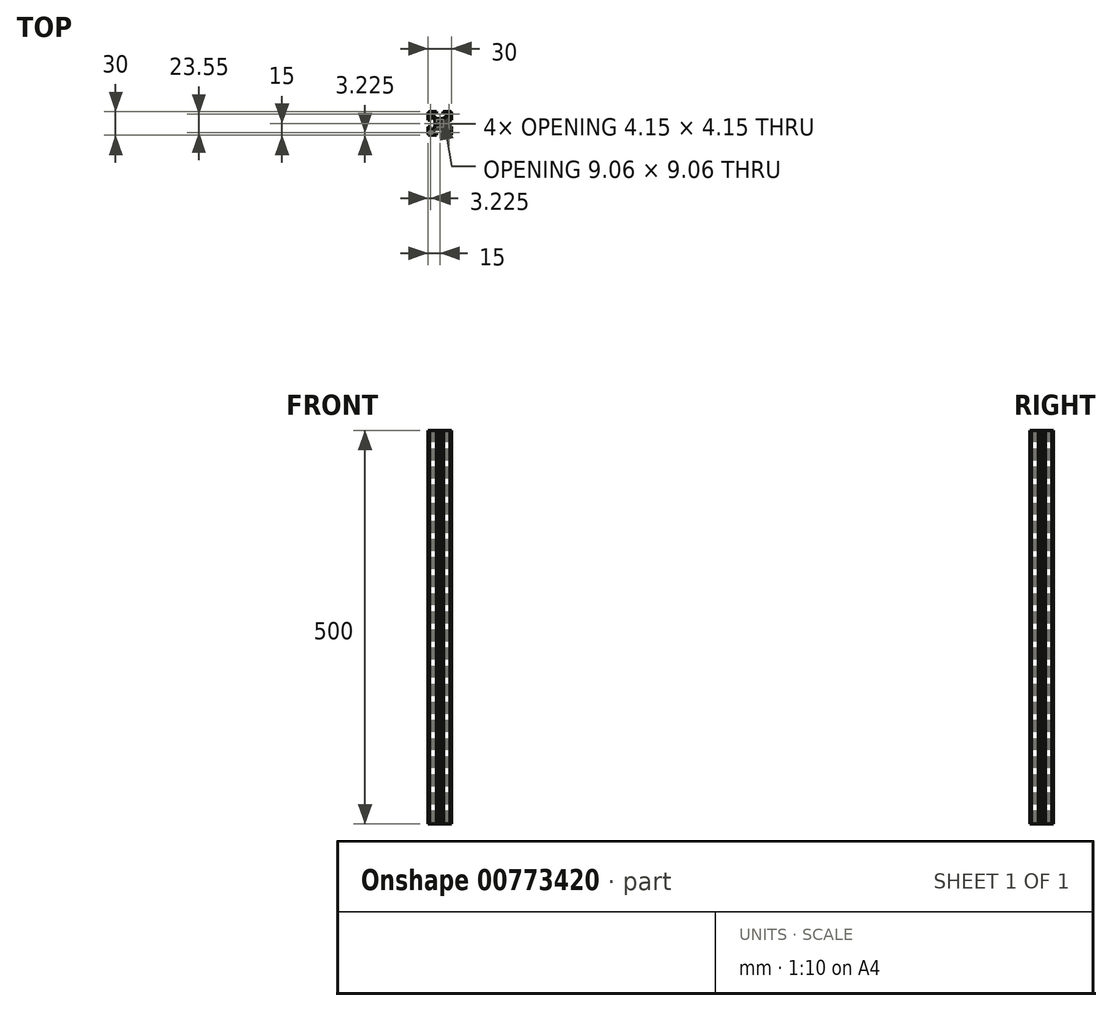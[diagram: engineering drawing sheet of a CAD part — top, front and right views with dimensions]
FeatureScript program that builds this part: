
annotation { "Feature Type Name" : "Feature", "Feature Type Description" : "" }
export const myFeature = defineFeature(function(context is Context, id is Id, definition is map)
    precondition{}
    {
        {
            var Q0;
            Q0=qCreatedBy(makeId("Top.planeOp"),FACE);
            var sketch = newSketch(context, id + "F0", { "sketchPlane" : qUnion([Q0])});
            skLineSegment(sketch, "E0", {"start": v(12.8, -8.25) * mm, "end": v(12.8, -4) * mm});
            skLineSegment(sketch, "E1", {"start": v(-12.8, 4) * mm, "end": v(-12.8, 8.25) * mm});
            skLineSegment(sketch, "E2", {"start": v(-13.85, -12.9) * mm, "end": v(-13.85, -12.85) * mm});
            skLineSegment(sketch, "E3", {"start": v(9.7, -12.9) * mm, "end": v(9.7, -12.85) * mm});
            skLineSegment(sketch, "E4", {"start": v(-9.7, -10.7) * mm, "end": v(-9.7, -10.66) * mm});
            skLineSegment(sketch, "E5", {"start": v(13.85, -10.7) * mm, "end": v(13.85, -10.66) * mm});
            skLineSegment(sketch, "E6", {"start": v(9.7, 10.66) * mm, "end": v(9.7, 10.7) * mm});
            skLineSegment(sketch, "E7", {"start": v(-13.85, 10.66) * mm, "end": v(-13.85, 10.7) * mm});
            skLineSegment(sketch, "E8", {"start": v(13.85, 12.85) * mm, "end": v(13.85, 12.9) * mm});
            skLineSegment(sketch, "E9", {"start": v(-9.7, 12.85) * mm, "end": v(-9.7, 12.9) * mm});
            skLineSegment(sketch, "E10", {"start": v(-15, -13.09) * mm, "end": v(-15, -13) * mm});
            skLineSegment(sketch, "E11", {"start": v(15, 13) * mm, "end": v(15, 13.09) * mm});
            skLineSegment(sketch, "E12", {"start": v(-3.64, -0.26) * mm, "end": v(-3.65, -0.09) * mm});
            skLineSegment(sketch, "E13", {"start": v(3.65, 0.09) * mm, "end": v(3.64, 0.26) * mm});
            skLineSegment(sketch, "E14", {"start": v(9.7, -12.94) * mm, "end": v(9.7, -12.9) * mm});
            skLineSegment(sketch, "E15", {"start": v(-9.7, -10.66) * mm, "end": v(-9.7, -10.61) * mm});
            skLineSegment(sketch, "E16", {"start": v(9.7, 10.61) * mm, "end": v(9.7, 10.66) * mm});
            skLineSegment(sketch, "E17", {"start": v(-9.7, 12.9) * mm, "end": v(-9.7, 12.94) * mm});
            skLineSegment(sketch, "E18", {"start": v(-15, -13.18) * mm, "end": v(-15, -13.09) * mm});
            skLineSegment(sketch, "E19", {"start": v(15, 13.09) * mm, "end": v(15, 13.18) * mm});
            skLineSegment(sketch, "E20", {"start": v(-13.85, -12.94) * mm, "end": v(-13.85, -12.9) * mm});
            skLineSegment(sketch, "E21", {"start": v(13.85, -10.66) * mm, "end": v(13.85, -10.61) * mm});
            skLineSegment(sketch, "E22", {"start": v(-13.85, 10.61) * mm, "end": v(-13.85, 10.66) * mm});
            skLineSegment(sketch, "E23", {"start": v(13.85, 12.9) * mm, "end": v(13.85, 12.94) * mm});
            skLineSegment(sketch, "E24", {"start": v(-3.62, -0.44) * mm, "end": v(-3.64, -0.26) * mm});
            skLineSegment(sketch, "E25", {"start": v(3.64, 0.26) * mm, "end": v(3.62, 0.44) * mm});
            skLineSegment(sketch, "E26", {"start": v(13.85, -10.61) * mm, "end": v(13.84, -10.57) * mm});
            skLineSegment(sketch, "E27", {"start": v(-13.84, 10.57) * mm, "end": v(-13.85, 10.61) * mm});
            skLineSegment(sketch, "E28", {"start": v(-13.84, -12.98) * mm, "end": v(-13.85, -12.94) * mm});
            skLineSegment(sketch, "E29", {"start": v(13.85, 12.94) * mm, "end": v(13.84, 12.98) * mm});
            skLineSegment(sketch, "E30", {"start": v(-14.98, -13.27) * mm, "end": v(-15, -13.18) * mm});
            skLineSegment(sketch, "E31", {"start": v(15, 13.18) * mm, "end": v(14.98, 13.27) * mm});
            skLineSegment(sketch, "E32", {"start": v(-9.7, -10.61) * mm, "end": v(-9.7, -10.57) * mm});
            skLineSegment(sketch, "E33", {"start": v(9.7, 10.57) * mm, "end": v(9.7, 10.61) * mm});
            skLineSegment(sketch, "E34", {"start": v(9.7, -12.98) * mm, "end": v(9.7, -12.94) * mm});
            skLineSegment(sketch, "E35", {"start": v(-9.7, 12.94) * mm, "end": v(-9.7, 12.98) * mm});
            skLineSegment(sketch, "E36", {"start": v(-3.6, -0.61) * mm, "end": v(-3.62, -0.44) * mm});
            skLineSegment(sketch, "E37", {"start": v(3.62, 0.44) * mm, "end": v(3.6, 0.61) * mm});
            skLineSegment(sketch, "E38", {"start": v(-13.83, -13.03) * mm, "end": v(-13.84, -12.98) * mm});
            skLineSegment(sketch, "E39", {"start": v(9.72, -13.03) * mm, "end": v(9.7, -12.98) * mm});
            skLineSegment(sketch, "E40", {"start": v(13.84, 12.98) * mm, "end": v(13.83, 13.03) * mm});
            skLineSegment(sketch, "E41", {"start": v(-9.7, 12.98) * mm, "end": v(-9.72, 13.03) * mm});
            skLineSegment(sketch, "E42", {"start": v(-14.97, -13.36) * mm, "end": v(-14.98, -13.27) * mm});
            skLineSegment(sketch, "E43", {"start": v(14.98, 13.27) * mm, "end": v(14.97, 13.36) * mm});
            skLineSegment(sketch, "E44", {"start": v(-9.7, -10.57) * mm, "end": v(-9.72, -10.52) * mm});
            skLineSegment(sketch, "E45", {"start": v(13.84, -10.57) * mm, "end": v(13.83, -10.52) * mm});
            skLineSegment(sketch, "E46", {"start": v(9.72, 10.52) * mm, "end": v(9.7, 10.57) * mm});
            skLineSegment(sketch, "E47", {"start": v(-13.83, 10.52) * mm, "end": v(-13.84, 10.57) * mm});
            skLineSegment(sketch, "E48", {"start": v(-3.56, -0.79) * mm, "end": v(-3.6, -0.61) * mm});
            skLineSegment(sketch, "E49", {"start": v(3.6, 0.61) * mm, "end": v(3.56, 0.79) * mm});
            skLineSegment(sketch, "E50", {"start": v(-14.95, -13.45) * mm, "end": v(-14.97, -13.36) * mm});
            skLineSegment(sketch, "E51", {"start": v(14.97, 13.36) * mm, "end": v(14.95, 13.45) * mm});
            skLineSegment(sketch, "E52", {"start": v(-13.82, -13.07) * mm, "end": v(-13.83, -13.03) * mm});
            skLineSegment(sketch, "E53", {"start": v(9.73, -13.07) * mm, "end": v(9.72, -13.03) * mm});
            skLineSegment(sketch, "E54", {"start": v(-9.72, -10.52) * mm, "end": v(-9.73, -10.48) * mm});
            skLineSegment(sketch, "E55", {"start": v(13.83, -10.52) * mm, "end": v(13.82, -10.48) * mm});
            skLineSegment(sketch, "E56", {"start": v(9.73, 10.48) * mm, "end": v(9.72, 10.52) * mm});
            skLineSegment(sketch, "E57", {"start": v(-13.82, 10.48) * mm, "end": v(-13.83, 10.52) * mm});
            skLineSegment(sketch, "E58", {"start": v(13.83, 13.03) * mm, "end": v(13.82, 13.07) * mm});
            skLineSegment(sketch, "E59", {"start": v(-9.72, 13.03) * mm, "end": v(-9.73, 13.07) * mm});
            skLineSegment(sketch, "E60", {"start": v(-3.52, -0.96) * mm, "end": v(-3.56, -0.79) * mm});
            skLineSegment(sketch, "E61", {"start": v(3.56, 0.79) * mm, "end": v(3.52, 0.96) * mm});
            skLineSegment(sketch, "E62", {"start": v(-14.93, -13.53) * mm, "end": v(-14.95, -13.45) * mm});
            skLineSegment(sketch, "E63", {"start": v(-9.73, -10.48) * mm, "end": v(-9.74, -10.43) * mm});
            skLineSegment(sketch, "E64", {"start": v(13.82, -10.48) * mm, "end": v(13.81, -10.43) * mm});
            skLineSegment(sketch, "E65", {"start": v(9.74, 10.43) * mm, "end": v(9.73, 10.48) * mm});
            skLineSegment(sketch, "E66", {"start": v(-13.81, 10.43) * mm, "end": v(-13.82, 10.48) * mm});
            skLineSegment(sketch, "E67", {"start": v(14.95, 13.45) * mm, "end": v(14.93, 13.53) * mm});
            skLineSegment(sketch, "E68", {"start": v(-13.81, -13.12) * mm, "end": v(-13.82, -13.07) * mm});
            skLineSegment(sketch, "E69", {"start": v(9.74, -13.12) * mm, "end": v(9.73, -13.07) * mm});
            skLineSegment(sketch, "E70", {"start": v(13.82, 13.07) * mm, "end": v(13.81, 13.12) * mm});
            skLineSegment(sketch, "E71", {"start": v(-9.73, 13.07) * mm, "end": v(-9.74, 13.12) * mm});
            skLineSegment(sketch, "E72", {"start": v(-3.47, -1.13) * mm, "end": v(-3.52, -0.96) * mm});
            skLineSegment(sketch, "E73", {"start": v(3.52, 0.96) * mm, "end": v(3.47, 1.13) * mm});
            skLineSegment(sketch, "E74", {"start": v(-13.8, -13.16) * mm, "end": v(-13.81, -13.12) * mm});
            skLineSegment(sketch, "E75", {"start": v(9.75, -13.16) * mm, "end": v(9.74, -13.12) * mm});
            skLineSegment(sketch, "E76", {"start": v(13.81, 13.12) * mm, "end": v(13.8, 13.16) * mm});
            skLineSegment(sketch, "E77", {"start": v(-9.74, 13.12) * mm, "end": v(-9.75, 13.16) * mm});
            skLineSegment(sketch, "E78", {"start": v(-9.74, -10.43) * mm, "end": v(-9.75, -10.4) * mm});
            skLineSegment(sketch, "E79", {"start": v(13.81, -10.43) * mm, "end": v(13.8, -10.4) * mm});
            skLineSegment(sketch, "E80", {"start": v(9.75, 10.4) * mm, "end": v(9.74, 10.43) * mm});
            skLineSegment(sketch, "E81", {"start": v(-13.8, 10.4) * mm, "end": v(-13.81, 10.43) * mm});
            skLineSegment(sketch, "E82", {"start": v(-14.9, -13.62) * mm, "end": v(-14.93, -13.53) * mm});
            skLineSegment(sketch, "E83", {"start": v(14.93, 13.53) * mm, "end": v(14.9, 13.62) * mm});
            skLineSegment(sketch, "E84", {"start": v(-14.87, -13.7) * mm, "end": v(-14.9, -13.62) * mm});
            skLineSegment(sketch, "E85", {"start": v(14.9, 13.62) * mm, "end": v(14.87, 13.7) * mm});
            skLineSegment(sketch, "E86", {"start": v(-13.79, -13.2) * mm, "end": v(-13.8, -13.16) * mm});
            skLineSegment(sketch, "E87", {"start": v(9.76, -13.2) * mm, "end": v(9.75, -13.16) * mm});
            skLineSegment(sketch, "E88", {"start": v(-9.75, -10.4) * mm, "end": v(-9.76, -10.35) * mm});
            skLineSegment(sketch, "E89", {"start": v(13.8, -10.4) * mm, "end": v(13.79, -10.35) * mm});
            skLineSegment(sketch, "E90", {"start": v(9.76, 10.35) * mm, "end": v(9.75, 10.4) * mm});
            skLineSegment(sketch, "E91", {"start": v(-13.79, 10.35) * mm, "end": v(-13.8, 10.4) * mm});
            skLineSegment(sketch, "E92", {"start": v(13.8, 13.16) * mm, "end": v(13.79, 13.2) * mm});
            skLineSegment(sketch, "E93", {"start": v(-9.75, 13.16) * mm, "end": v(-9.76, 13.2) * mm});
            skLineSegment(sketch, "E94", {"start": v(-3.41, -1.3) * mm, "end": v(-3.47, -1.13) * mm});
            skLineSegment(sketch, "E95", {"start": v(3.47, 1.13) * mm, "end": v(3.41, 1.3) * mm});
            skLineSegment(sketch, "E96", {"start": v(-14.84, -13.79) * mm, "end": v(-14.87, -13.7) * mm});
            skLineSegment(sketch, "E97", {"start": v(14.87, 13.7) * mm, "end": v(14.84, 13.79) * mm});
            skLineSegment(sketch, "E98", {"start": v(9.78, -13.24) * mm, "end": v(9.76, -13.2) * mm});
            skLineSegment(sketch, "E99", {"start": v(-9.76, -10.35) * mm, "end": v(-9.78, -10.3) * mm});
            skLineSegment(sketch, "E100", {"start": v(9.78, 10.3) * mm, "end": v(9.76, 10.35) * mm});
            skLineSegment(sketch, "E101", {"start": v(-9.76, 13.2) * mm, "end": v(-9.78, 13.24) * mm});
            skLineSegment(sketch, "E102", {"start": v(-13.77, -13.24) * mm, "end": v(-13.79, -13.2) * mm});
            skLineSegment(sketch, "E103", {"start": v(13.79, -10.35) * mm, "end": v(13.77, -10.3) * mm});
            skLineSegment(sketch, "E104", {"start": v(-13.77, 10.3) * mm, "end": v(-13.79, 10.35) * mm});
            skLineSegment(sketch, "E105", {"start": v(13.79, 13.2) * mm, "end": v(13.77, 13.24) * mm});
            skLineSegment(sketch, "E106", {"start": v(-3.35, -1.46) * mm, "end": v(-3.41, -1.3) * mm});
            skLineSegment(sketch, "E107", {"start": v(3.41, 1.3) * mm, "end": v(3.35, 1.46) * mm});
            skLineSegment(sketch, "E108", {"start": v(-13.75, -13.28) * mm, "end": v(-13.77, -13.24) * mm});
            skLineSegment(sketch, "E109", {"start": v(13.77, -10.3) * mm, "end": v(13.75, -10.27) * mm});
            skLineSegment(sketch, "E110", {"start": v(-13.75, 10.27) * mm, "end": v(-13.77, 10.3) * mm});
            skLineSegment(sketch, "E111", {"start": v(13.77, 13.24) * mm, "end": v(13.75, 13.28) * mm});
            skLineSegment(sketch, "E112", {"start": v(9.8, -13.28) * mm, "end": v(9.78, -13.24) * mm});
            skLineSegment(sketch, "E113", {"start": v(-9.78, -10.3) * mm, "end": v(-9.8, -10.27) * mm});
            skLineSegment(sketch, "E114", {"start": v(9.8, 10.27) * mm, "end": v(9.78, 10.3) * mm});
            skLineSegment(sketch, "E115", {"start": v(-9.78, 13.24) * mm, "end": v(-9.8, 13.28) * mm});
            skLineSegment(sketch, "E116", {"start": v(-14.8, -13.87) * mm, "end": v(-14.84, -13.79) * mm});
            skLineSegment(sketch, "E117", {"start": v(14.84, 13.79) * mm, "end": v(14.8, 13.87) * mm});
            skLineSegment(sketch, "E118", {"start": v(-3.27, -1.62) * mm, "end": v(-3.35, -1.46) * mm});
            skLineSegment(sketch, "E119", {"start": v(3.35, 1.46) * mm, "end": v(3.27, 1.62) * mm});
            skLineSegment(sketch, "E120", {"start": v(-13.73, -13.32) * mm, "end": v(-13.75, -13.28) * mm});
            skLineSegment(sketch, "E121", {"start": v(13.75, -10.27) * mm, "end": v(13.73, -10.23) * mm});
            skLineSegment(sketch, "E122", {"start": v(-13.73, 10.23) * mm, "end": v(-13.75, 10.27) * mm});
            skLineSegment(sketch, "E123", {"start": v(13.75, 13.28) * mm, "end": v(13.73, 13.32) * mm});
            skLineSegment(sketch, "E124", {"start": v(-14.76, -13.95) * mm, "end": v(-14.8, -13.87) * mm});
            skLineSegment(sketch, "E125", {"start": v(14.8, 13.87) * mm, "end": v(14.76, 13.95) * mm});
            skLineSegment(sketch, "E126", {"start": v(9.82, -13.32) * mm, "end": v(9.8, -13.28) * mm});
            skLineSegment(sketch, "E127", {"start": v(-9.8, -10.27) * mm, "end": v(-9.82, -10.23) * mm});
            skLineSegment(sketch, "E128", {"start": v(9.82, 10.23) * mm, "end": v(9.8, 10.27) * mm});
            skLineSegment(sketch, "E129", {"start": v(-9.8, 13.28) * mm, "end": v(-9.82, 13.32) * mm});
            skLineSegment(sketch, "E130", {"start": v(-9.82, -10.23) * mm, "end": v(-9.84, -10.19) * mm});
            skLineSegment(sketch, "E131", {"start": v(9.84, 10.19) * mm, "end": v(9.82, 10.23) * mm});
            skLineSegment(sketch, "E132", {"start": v(9.84, -13.36) * mm, "end": v(9.82, -13.32) * mm});
            skLineSegment(sketch, "E133", {"start": v(-9.82, 13.32) * mm, "end": v(-9.84, 13.36) * mm});
            skLineSegment(sketch, "E134", {"start": v(-14.72, -14.03) * mm, "end": v(-14.76, -13.95) * mm});
            skLineSegment(sketch, "E135", {"start": v(14.76, 13.95) * mm, "end": v(14.72, 14.03) * mm});
            skLineSegment(sketch, "E136", {"start": v(13.73, -10.23) * mm, "end": v(13.7, -10.19) * mm});
            skLineSegment(sketch, "E137", {"start": v(-13.7, 10.19) * mm, "end": v(-13.73, 10.23) * mm});
            skLineSegment(sketch, "E138", {"start": v(-13.7, -13.36) * mm, "end": v(-13.73, -13.32) * mm});
            skLineSegment(sketch, "E139", {"start": v(13.73, 13.32) * mm, "end": v(13.7, 13.36) * mm});
            skLineSegment(sketch, "E140", {"start": v(6, -0.92) * mm, "end": v(5.47, 0) * mm});
            skLineSegment(sketch, "E141", {"start": v(-5.47, 0) * mm, "end": v(-6, 0.92) * mm});
            skLineSegment(sketch, "E142", {"start": v(-13.68, -13.4) * mm, "end": v(-13.7, -13.36) * mm});
            skLineSegment(sketch, "E143", {"start": v(13.7, 13.36) * mm, "end": v(13.68, 13.4) * mm});
            skLineSegment(sketch, "E144", {"start": v(13.7, -10.19) * mm, "end": v(13.68, -10.15) * mm});
            skLineSegment(sketch, "E145", {"start": v(-13.68, 10.15) * mm, "end": v(-13.7, 10.19) * mm});
            skLineSegment(sketch, "E146", {"start": v(-14.67, -14.1) * mm, "end": v(-14.72, -14.03) * mm});
            skLineSegment(sketch, "E147", {"start": v(14.72, 14.03) * mm, "end": v(14.67, 14.1) * mm});
            skLineSegment(sketch, "E148", {"start": v(9.87, -13.4) * mm, "end": v(9.84, -13.36) * mm});
            skLineSegment(sketch, "E149", {"start": v(-9.84, 13.36) * mm, "end": v(-9.87, 13.4) * mm});
            skLineSegment(sketch, "E150", {"start": v(-9.84, -10.19) * mm, "end": v(-9.87, -10.15) * mm});
            skLineSegment(sketch, "E151", {"start": v(9.87, 10.15) * mm, "end": v(9.84, 10.19) * mm});
            skLineSegment(sketch, "E152", {"start": v(-13.66, -13.44) * mm, "end": v(-13.68, -13.4) * mm});
            skLineSegment(sketch, "E153", {"start": v(9.9, -13.44) * mm, "end": v(9.87, -13.4) * mm});
            skLineSegment(sketch, "E154", {"start": v(-9.87, -10.15) * mm, "end": v(-9.9, -10.11) * mm});
            skLineSegment(sketch, "E155", {"start": v(13.68, -10.15) * mm, "end": v(13.66, -10.11) * mm});
            skLineSegment(sketch, "E156", {"start": v(9.9, 10.11) * mm, "end": v(9.87, 10.15) * mm});
            skLineSegment(sketch, "E157", {"start": v(-13.66, 10.11) * mm, "end": v(-13.68, 10.15) * mm});
            skLineSegment(sketch, "E158", {"start": v(13.68, 13.4) * mm, "end": v(13.66, 13.44) * mm});
            skLineSegment(sketch, "E159", {"start": v(-9.87, 13.4) * mm, "end": v(-9.9, 13.44) * mm});
            skLineSegment(sketch, "E160", {"start": v(-14.62, -14.18) * mm, "end": v(-14.67, -14.1) * mm});
            skLineSegment(sketch, "E161", {"start": v(14.67, 14.1) * mm, "end": v(14.62, 14.18) * mm});
            skLineSegment(sketch, "E162", {"start": v(-4.36, -3.35) * mm, "end": v(-4.53, -3.12) * mm});
            skLineSegment(sketch, "E163", {"start": v(4.53, 3.12) * mm, "end": v(4.36, 3.35) * mm});
            skLineSegment(sketch, "E164", {"start": v(9.92, -13.47) * mm, "end": v(9.9, -13.44) * mm});
            skLineSegment(sketch, "E165", {"start": v(-9.9, -10.11) * mm, "end": v(-9.92, -10.08) * mm});
            skLineSegment(sketch, "E166", {"start": v(9.92, 10.08) * mm, "end": v(9.9, 10.11) * mm});
            skLineSegment(sketch, "E167", {"start": v(-9.9, 13.44) * mm, "end": v(-9.92, 13.47) * mm});
            skLineSegment(sketch, "E168", {"start": v(-14.56, -14.25) * mm, "end": v(-14.62, -14.18) * mm});
            skLineSegment(sketch, "E169", {"start": v(14.62, 14.18) * mm, "end": v(14.56, 14.25) * mm});
            skLineSegment(sketch, "E170", {"start": v(-13.63, -13.47) * mm, "end": v(-13.66, -13.44) * mm});
            skLineSegment(sketch, "E171", {"start": v(13.66, -10.11) * mm, "end": v(13.63, -10.08) * mm});
            skLineSegment(sketch, "E172", {"start": v(-13.63, 10.08) * mm, "end": v(-13.66, 10.11) * mm});
            skLineSegment(sketch, "E173", {"start": v(13.66, 13.44) * mm, "end": v(13.63, 13.47) * mm});
            skLineSegment(sketch, "E174", {"start": v(-4.18, -3.57) * mm, "end": v(-4.36, -3.35) * mm});
            skLineSegment(sketch, "E175", {"start": v(4.36, 3.35) * mm, "end": v(4.18, 3.57) * mm});
            skLineSegment(sketch, "E176", {"start": v(-14.5, -14.32) * mm, "end": v(-14.56, -14.25) * mm});
            skLineSegment(sketch, "E177", {"start": v(13.63, -10.08) * mm, "end": v(13.6, -10.04) * mm});
            skLineSegment(sketch, "E178", {"start": v(-13.6, 10.04) * mm, "end": v(-13.63, 10.08) * mm});
            skLineSegment(sketch, "E179", {"start": v(14.56, 14.25) * mm, "end": v(14.5, 14.32) * mm});
            skLineSegment(sketch, "E180", {"start": v(-13.6, -13.5) * mm, "end": v(-13.63, -13.47) * mm});
            skLineSegment(sketch, "E181", {"start": v(13.63, 13.47) * mm, "end": v(13.6, 13.5) * mm});
            skLineSegment(sketch, "E182", {"start": v(-9.92, -10.08) * mm, "end": v(-9.95, -10.04) * mm});
            skLineSegment(sketch, "E183", {"start": v(9.95, 10.04) * mm, "end": v(9.92, 10.08) * mm});
            skLineSegment(sketch, "E184", {"start": v(9.95, -13.5) * mm, "end": v(9.92, -13.47) * mm});
            skLineSegment(sketch, "E185", {"start": v(-9.92, 13.47) * mm, "end": v(-9.95, 13.5) * mm});
            skLineSegment(sketch, "E186", {"start": v(4.53, -3.12) * mm, "end": v(3.27, -1.62) * mm});
            skLineSegment(sketch, "E187", {"start": v(-3.27, 1.62) * mm, "end": v(-4.53, 3.12) * mm});
            skLineSegment(sketch, "E188", {"start": v(-3.99, -3.79) * mm, "end": v(-4.18, -3.57) * mm});
            skLineSegment(sketch, "E189", {"start": v(4.18, 3.57) * mm, "end": v(3.99, 3.79) * mm});
            skLineSegment(sketch, "E190", {"start": v(-13.57, -13.54) * mm, "end": v(-13.6, -13.5) * mm});
            skLineSegment(sketch, "E191", {"start": v(9.98, -13.54) * mm, "end": v(9.95, -13.5) * mm});
            skLineSegment(sketch, "E192", {"start": v(-9.95, -10.04) * mm, "end": v(-9.98, -10) * mm});
            skLineSegment(sketch, "E193", {"start": v(13.6, -10.04) * mm, "end": v(13.57, -10) * mm});
            skLineSegment(sketch, "E194", {"start": v(9.98, 10) * mm, "end": v(9.95, 10.04) * mm});
            skLineSegment(sketch, "E195", {"start": v(-13.57, 10) * mm, "end": v(-13.6, 10.04) * mm});
            skLineSegment(sketch, "E196", {"start": v(13.6, 13.5) * mm, "end": v(13.57, 13.54) * mm});
            skLineSegment(sketch, "E197", {"start": v(-9.95, 13.5) * mm, "end": v(-9.98, 13.54) * mm});
            skLineSegment(sketch, "E198", {"start": v(-14.45, -14.38) * mm, "end": v(-14.5, -14.32) * mm});
            skLineSegment(sketch, "E199", {"start": v(14.5, 14.32) * mm, "end": v(14.45, 14.38) * mm});
            skLineSegment(sketch, "E200", {"start": v(10, -13.57) * mm, "end": v(9.98, -13.54) * mm});
            skLineSegment(sketch, "E201", {"start": v(-9.98, 13.54) * mm, "end": v(-10, 13.57) * mm});
            skLineSegment(sketch, "E202", {"start": v(-14.38, -14.45) * mm, "end": v(-14.45, -14.38) * mm});
            skLineSegment(sketch, "E203", {"start": v(-13.54, -13.57) * mm, "end": v(-13.57, -13.54) * mm});
            skLineSegment(sketch, "E204", {"start": v(8.25, -10.05) * mm, "end": v(4.2, -6) * mm});
            skLineSegment(sketch, "E205", {"start": v(-9.98, -10) * mm, "end": v(-10, -9.98) * mm});
            skLineSegment(sketch, "E206", {"start": v(10.05, -8.25) * mm, "end": v(6, -4.2) * mm});
            skLineSegment(sketch, "E207", {"start": v(-3.79, -3.99) * mm, "end": v(-3.99, -3.79) * mm});
            skLineSegment(sketch, "E208", {"start": v(3.99, 3.79) * mm, "end": v(3.79, 3.99) * mm});
            skLineSegment(sketch, "E209", {"start": v(-6, 4.2) * mm, "end": v(-10.05, 8.25) * mm});
            skLineSegment(sketch, "E210", {"start": v(-4.2, 6) * mm, "end": v(-8.25, 10.05) * mm});
            skLineSegment(sketch, "E211", {"start": v(10, 9.98) * mm, "end": v(9.98, 10) * mm});
            skLineSegment(sketch, "E212", {"start": v(13.57, 13.54) * mm, "end": v(13.54, 13.57) * mm});
            skLineSegment(sketch, "E213", {"start": v(14.45, 14.38) * mm, "end": v(14.38, 14.45) * mm});
            skLineSegment(sketch, "E214", {"start": v(13.57, -10) * mm, "end": v(13.54, -9.98) * mm});
            skLineSegment(sketch, "E215", {"start": v(-13.54, 9.98) * mm, "end": v(-13.57, 10) * mm});
            skLineSegment(sketch, "E216", {"start": v(-14.32, -14.5) * mm, "end": v(-14.38, -14.45) * mm});
            skLineSegment(sketch, "E217", {"start": v(14.38, 14.45) * mm, "end": v(14.32, 14.5) * mm});
            skLineSegment(sketch, "E218", {"start": v(-13.5, -13.6) * mm, "end": v(-13.54, -13.57) * mm});
            skLineSegment(sketch, "E219", {"start": v(10.04, -13.6) * mm, "end": v(10, -13.57) * mm});
            skLineSegment(sketch, "E220", {"start": v(-10, -9.98) * mm, "end": v(-10.04, -9.95) * mm});
            skLineSegment(sketch, "E221", {"start": v(13.54, -9.98) * mm, "end": v(13.5, -9.95) * mm});
            skLineSegment(sketch, "E222", {"start": v(10.04, 9.95) * mm, "end": v(10, 9.98) * mm});
            skLineSegment(sketch, "E223", {"start": v(-13.5, 9.95) * mm, "end": v(-13.54, 9.98) * mm});
            skLineSegment(sketch, "E224", {"start": v(13.54, 13.57) * mm, "end": v(13.5, 13.6) * mm});
            skLineSegment(sketch, "E225", {"start": v(-10, 13.57) * mm, "end": v(-10.04, 13.6) * mm});
            skLineSegment(sketch, "E226", {"start": v(-3.57, -4.18) * mm, "end": v(-3.79, -3.99) * mm});
            skLineSegment(sketch, "E227", {"start": v(3.79, 3.99) * mm, "end": v(3.57, 4.18) * mm});
            skLineSegment(sketch, "E228", {"start": v(3.12, -4.53) * mm, "end": v(1.62, -3.27) * mm});
            skLineSegment(sketch, "E229", {"start": v(-1.62, 3.27) * mm, "end": v(-3.12, 4.53) * mm});
            skLineSegment(sketch, "E230", {"start": v(13.5, -9.95) * mm, "end": v(13.47, -9.92) * mm});
            skLineSegment(sketch, "E231", {"start": v(-13.47, 9.92) * mm, "end": v(-13.5, 9.95) * mm});
            skLineSegment(sketch, "E232", {"start": v(-10.04, -9.95) * mm, "end": v(-10.08, -9.92) * mm});
            skLineSegment(sketch, "E233", {"start": v(10.08, 9.92) * mm, "end": v(10.04, 9.95) * mm});
            skLineSegment(sketch, "E234", {"start": v(-13.47, -13.63) * mm, "end": v(-13.5, -13.6) * mm});
            skLineSegment(sketch, "E235", {"start": v(13.5, 13.6) * mm, "end": v(13.47, 13.63) * mm});
            skLineSegment(sketch, "E236", {"start": v(-14.25, -14.56) * mm, "end": v(-14.32, -14.5) * mm});
            skLineSegment(sketch, "E237", {"start": v(10.08, -13.63) * mm, "end": v(10.04, -13.6) * mm});
            skLineSegment(sketch, "E238", {"start": v(-10.04, 13.6) * mm, "end": v(-10.08, 13.63) * mm});
            skLineSegment(sketch, "E239", {"start": v(14.32, 14.5) * mm, "end": v(14.25, 14.56) * mm});
            skLineSegment(sketch, "E240", {"start": v(-3.35, -4.36) * mm, "end": v(-3.57, -4.18) * mm});
            skLineSegment(sketch, "E241", {"start": v(3.57, 4.18) * mm, "end": v(3.35, 4.36) * mm});
            skLineSegment(sketch, "E242", {"start": v(-13.44, -13.66) * mm, "end": v(-13.47, -13.63) * mm});
            skLineSegment(sketch, "E243", {"start": v(10.11, -13.66) * mm, "end": v(10.08, -13.63) * mm});
            skLineSegment(sketch, "E244", {"start": v(13.47, 13.63) * mm, "end": v(13.44, 13.66) * mm});
            skLineSegment(sketch, "E245", {"start": v(-10.08, 13.63) * mm, "end": v(-10.11, 13.66) * mm});
            skLineSegment(sketch, "E246", {"start": v(-14.18, -14.62) * mm, "end": v(-14.25, -14.56) * mm});
            skLineSegment(sketch, "E247", {"start": v(14.25, 14.56) * mm, "end": v(14.18, 14.62) * mm});
            skLineSegment(sketch, "E248", {"start": v(-10.08, -9.92) * mm, "end": v(-10.11, -9.9) * mm});
            skLineSegment(sketch, "E249", {"start": v(13.47, -9.92) * mm, "end": v(13.44, -9.9) * mm});
            skLineSegment(sketch, "E250", {"start": v(10.11, 9.9) * mm, "end": v(10.08, 9.92) * mm});
            skLineSegment(sketch, "E251", {"start": v(-13.44, 9.9) * mm, "end": v(-13.47, 9.92) * mm});
            skLineSegment(sketch, "E252", {"start": v(-3.12, -4.53) * mm, "end": v(-3.35, -4.36) * mm});
            skLineSegment(sketch, "E253", {"start": v(3.35, 4.36) * mm, "end": v(3.12, 4.53) * mm});
            skLineSegment(sketch, "E254", {"start": v(-14.1, -14.67) * mm, "end": v(-14.18, -14.62) * mm});
            skLineSegment(sketch, "E255", {"start": v(14.18, 14.62) * mm, "end": v(14.1, 14.67) * mm});
            skLineSegment(sketch, "E256", {"start": v(-13.4, -13.68) * mm, "end": v(-13.44, -13.66) * mm});
            skLineSegment(sketch, "E257", {"start": v(10.15, -13.68) * mm, "end": v(10.11, -13.66) * mm});
            skLineSegment(sketch, "E258", {"start": v(-10.11, -9.9) * mm, "end": v(-10.15, -9.87) * mm});
            skLineSegment(sketch, "E259", {"start": v(13.44, -9.9) * mm, "end": v(13.4, -9.87) * mm});
            skLineSegment(sketch, "E260", {"start": v(10.15, 9.87) * mm, "end": v(10.11, 9.9) * mm});
            skLineSegment(sketch, "E261", {"start": v(-13.4, 9.87) * mm, "end": v(-13.44, 9.9) * mm});
            skLineSegment(sketch, "E262", {"start": v(13.44, 13.66) * mm, "end": v(13.4, 13.68) * mm});
            skLineSegment(sketch, "E263", {"start": v(-10.11, 13.66) * mm, "end": v(-10.15, 13.68) * mm});
            skLineSegment(sketch, "E264", {"start": v(-10.15, -9.87) * mm, "end": v(-10.19, -9.84) * mm});
            skLineSegment(sketch, "E265", {"start": v(10.19, 9.84) * mm, "end": v(10.15, 9.87) * mm});
            skLineSegment(sketch, "E266", {"start": v(13.4, -9.87) * mm, "end": v(13.36, -9.84) * mm});
            skLineSegment(sketch, "E267", {"start": v(-13.36, 9.84) * mm, "end": v(-13.4, 9.87) * mm});
            skLineSegment(sketch, "E268", {"start": v(-14.03, -14.72) * mm, "end": v(-14.1, -14.67) * mm});
            skLineSegment(sketch, "E269", {"start": v(14.1, 14.67) * mm, "end": v(14.03, 14.72) * mm});
            skLineSegment(sketch, "E270", {"start": v(10.19, -13.7) * mm, "end": v(10.15, -13.68) * mm});
            skLineSegment(sketch, "E271", {"start": v(-10.15, 13.68) * mm, "end": v(-10.19, 13.7) * mm});
            skLineSegment(sketch, "E272", {"start": v(-13.36, -13.7) * mm, "end": v(-13.4, -13.68) * mm});
            skLineSegment(sketch, "E273", {"start": v(13.4, 13.68) * mm, "end": v(13.36, 13.7) * mm});
            skLineSegment(sketch, "E274", {"start": v(0.92, -6) * mm, "end": v(0, -5.47) * mm});
            skLineSegment(sketch, "E275", {"start": v(0, 5.47) * mm, "end": v(-0.92, 6) * mm});
            skLineSegment(sketch, "E276", {"start": v(-13.32, -13.73) * mm, "end": v(-13.36, -13.7) * mm});
            skLineSegment(sketch, "E277", {"start": v(13.36, 13.7) * mm, "end": v(13.32, 13.73) * mm});
            skLineSegment(sketch, "E278", {"start": v(10.23, -13.73) * mm, "end": v(10.19, -13.7) * mm});
            skLineSegment(sketch, "E279", {"start": v(-10.19, 13.7) * mm, "end": v(-10.23, 13.73) * mm});
            skLineSegment(sketch, "E280", {"start": v(-13.95, -14.76) * mm, "end": v(-14.03, -14.72) * mm});
            skLineSegment(sketch, "E281", {"start": v(14.03, 14.72) * mm, "end": v(13.95, 14.76) * mm});
            skLineSegment(sketch, "E282", {"start": v(13.36, -9.84) * mm, "end": v(13.32, -9.82) * mm});
            skLineSegment(sketch, "E283", {"start": v(-13.32, 9.82) * mm, "end": v(-13.36, 9.84) * mm});
            skLineSegment(sketch, "E284", {"start": v(-10.19, -9.84) * mm, "end": v(-10.23, -9.82) * mm});
            skLineSegment(sketch, "E285", {"start": v(10.23, 9.82) * mm, "end": v(10.19, 9.84) * mm});
            skLineSegment(sketch, "E286", {"start": v(-10.23, -9.82) * mm, "end": v(-10.27, -9.8) * mm});
            skLineSegment(sketch, "E287", {"start": v(13.32, -9.82) * mm, "end": v(13.28, -9.8) * mm});
            skLineSegment(sketch, "E288", {"start": v(10.27, 9.8) * mm, "end": v(10.23, 9.82) * mm});
            skLineSegment(sketch, "E289", {"start": v(-13.28, 9.8) * mm, "end": v(-13.32, 9.82) * mm});
            skLineSegment(sketch, "E290", {"start": v(-13.87, -14.8) * mm, "end": v(-13.95, -14.76) * mm});
            skLineSegment(sketch, "E291", {"start": v(13.95, 14.76) * mm, "end": v(13.87, 14.8) * mm});
            skLineSegment(sketch, "E292", {"start": v(-13.28, -13.75) * mm, "end": v(-13.32, -13.73) * mm});
            skLineSegment(sketch, "E293", {"start": v(10.27, -13.75) * mm, "end": v(10.23, -13.73) * mm});
            skLineSegment(sketch, "E294", {"start": v(13.32, 13.73) * mm, "end": v(13.28, 13.75) * mm});
            skLineSegment(sketch, "E295", {"start": v(-10.23, 13.73) * mm, "end": v(-10.27, 13.75) * mm});
            skLineSegment(sketch, "E296", {"start": v(-1.46, -3.35) * mm, "end": v(-1.62, -3.27) * mm});
            skLineSegment(sketch, "E297", {"start": v(1.62, 3.27) * mm, "end": v(1.46, 3.35) * mm});
            skLineSegment(sketch, "E298", {"start": v(-13.79, -14.84) * mm, "end": v(-13.87, -14.8) * mm});
            skLineSegment(sketch, "E299", {"start": v(13.87, 14.8) * mm, "end": v(13.79, 14.84) * mm});
            skLineSegment(sketch, "E300", {"start": v(-10.27, -9.8) * mm, "end": v(-10.3, -9.78) * mm});
            skLineSegment(sketch, "E301", {"start": v(13.28, -9.8) * mm, "end": v(13.24, -9.78) * mm});
            skLineSegment(sketch, "E302", {"start": v(10.3, 9.78) * mm, "end": v(10.27, 9.8) * mm});
            skLineSegment(sketch, "E303", {"start": v(-13.24, 9.78) * mm, "end": v(-13.28, 9.8) * mm});
            skLineSegment(sketch, "E304", {"start": v(-13.24, -13.77) * mm, "end": v(-13.28, -13.75) * mm});
            skLineSegment(sketch, "E305", {"start": v(10.3, -13.77) * mm, "end": v(10.27, -13.75) * mm});
            skLineSegment(sketch, "E306", {"start": v(13.28, 13.75) * mm, "end": v(13.24, 13.77) * mm});
            skLineSegment(sketch, "E307", {"start": v(-10.27, 13.75) * mm, "end": v(-10.3, 13.77) * mm});
            skLineSegment(sketch, "E308", {"start": v(-1.3, -3.41) * mm, "end": v(-1.46, -3.35) * mm});
            skLineSegment(sketch, "E309", {"start": v(1.46, 3.35) * mm, "end": v(1.3, 3.41) * mm});
            skLineSegment(sketch, "E310", {"start": v(-13.2, -13.79) * mm, "end": v(-13.24, -13.77) * mm});
            skLineSegment(sketch, "E311", {"start": v(10.35, -13.79) * mm, "end": v(10.3, -13.77) * mm});
            skLineSegment(sketch, "E312", {"start": v(13.24, 13.77) * mm, "end": v(13.2, 13.79) * mm});
            skLineSegment(sketch, "E313", {"start": v(-10.3, 13.77) * mm, "end": v(-10.35, 13.79) * mm});
            skLineSegment(sketch, "E314", {"start": v(-10.3, -9.78) * mm, "end": v(-10.35, -9.76) * mm});
            skLineSegment(sketch, "E315", {"start": v(13.24, -9.78) * mm, "end": v(13.2, -9.76) * mm});
            skLineSegment(sketch, "E316", {"start": v(10.35, 9.76) * mm, "end": v(10.3, 9.78) * mm});
            skLineSegment(sketch, "E317", {"start": v(-13.2, 9.76) * mm, "end": v(-13.24, 9.78) * mm});
            skLineSegment(sketch, "E318", {"start": v(-13.7, -14.87) * mm, "end": v(-13.79, -14.84) * mm});
            skLineSegment(sketch, "E319", {"start": v(13.79, 14.84) * mm, "end": v(13.7, 14.87) * mm});
            skLineSegment(sketch, "E320", {"start": v(-1.13, -3.47) * mm, "end": v(-1.3, -3.41) * mm});
            skLineSegment(sketch, "E321", {"start": v(1.3, 3.41) * mm, "end": v(1.13, 3.47) * mm});
            skLineSegment(sketch, "E322", {"start": v(-13.16, -13.8) * mm, "end": v(-13.2, -13.79) * mm});
            skLineSegment(sketch, "E323", {"start": v(10.4, -13.8) * mm, "end": v(10.35, -13.79) * mm});
            skLineSegment(sketch, "E324", {"start": v(-10.35, -9.76) * mm, "end": v(-10.4, -9.75) * mm});
            skLineSegment(sketch, "E325", {"start": v(13.2, -9.76) * mm, "end": v(13.16, -9.75) * mm});
            skLineSegment(sketch, "E326", {"start": v(10.4, 9.75) * mm, "end": v(10.35, 9.76) * mm});
            skLineSegment(sketch, "E327", {"start": v(-13.16, 9.75) * mm, "end": v(-13.2, 9.76) * mm});
            skLineSegment(sketch, "E328", {"start": v(13.2, 13.79) * mm, "end": v(13.16, 13.8) * mm});
            skLineSegment(sketch, "E329", {"start": v(-10.35, 13.79) * mm, "end": v(-10.4, 13.8) * mm});
            skLineSegment(sketch, "E330", {"start": v(-13.62, -14.9) * mm, "end": v(-13.7, -14.87) * mm});
            skLineSegment(sketch, "E331", {"start": v(13.7, 14.87) * mm, "end": v(13.62, 14.9) * mm});
            skLineSegment(sketch, "E332", {"start": v(-13.53, -14.93) * mm, "end": v(-13.62, -14.9) * mm});
            skLineSegment(sketch, "E333", {"start": v(13.62, 14.9) * mm, "end": v(13.53, 14.93) * mm});
            skLineSegment(sketch, "E334", {"start": v(10.43, -13.81) * mm, "end": v(10.4, -13.8) * mm});
            skLineSegment(sketch, "E335", {"start": v(-10.4, -9.75) * mm, "end": v(-10.43, -9.74) * mm});
            skLineSegment(sketch, "E336", {"start": v(10.43, 9.74) * mm, "end": v(10.4, 9.75) * mm});
            skLineSegment(sketch, "E337", {"start": v(-10.4, 13.8) * mm, "end": v(-10.43, 13.81) * mm});
            skLineSegment(sketch, "E338", {"start": v(-13.12, -13.81) * mm, "end": v(-13.16, -13.8) * mm});
            skLineSegment(sketch, "E339", {"start": v(13.16, -9.75) * mm, "end": v(13.12, -9.74) * mm});
            skLineSegment(sketch, "E340", {"start": v(-13.12, 9.74) * mm, "end": v(-13.16, 9.75) * mm});
            skLineSegment(sketch, "E341", {"start": v(13.16, 13.8) * mm, "end": v(13.12, 13.81) * mm});
            skLineSegment(sketch, "E342", {"start": v(-0.96, -3.52) * mm, "end": v(-1.13, -3.47) * mm});
            skLineSegment(sketch, "E343", {"start": v(1.13, 3.47) * mm, "end": v(0.96, 3.52) * mm});
            skLineSegment(sketch, "E344", {"start": v(-13.07, -13.82) * mm, "end": v(-13.12, -13.81) * mm});
            skLineSegment(sketch, "E345", {"start": v(13.12, -9.74) * mm, "end": v(13.07, -9.73) * mm});
            skLineSegment(sketch, "E346", {"start": v(-13.07, 9.73) * mm, "end": v(-13.12, 9.74) * mm});
            skLineSegment(sketch, "E347", {"start": v(13.12, 13.81) * mm, "end": v(13.07, 13.82) * mm});
            skLineSegment(sketch, "E348", {"start": v(-13.45, -14.95) * mm, "end": v(-13.53, -14.93) * mm});
            skLineSegment(sketch, "E349", {"start": v(10.48, -13.82) * mm, "end": v(10.43, -13.81) * mm});
            skLineSegment(sketch, "E350", {"start": v(-10.43, -9.74) * mm, "end": v(-10.48, -9.73) * mm});
            skLineSegment(sketch, "E351", {"start": v(10.48, 9.73) * mm, "end": v(10.43, 9.74) * mm});
            skLineSegment(sketch, "E352", {"start": v(-10.43, 13.81) * mm, "end": v(-10.48, 13.82) * mm});
            skLineSegment(sketch, "E353", {"start": v(13.53, 14.93) * mm, "end": v(13.45, 14.95) * mm});
            skLineSegment(sketch, "E354", {"start": v(-0.79, -3.56) * mm, "end": v(-0.96, -3.52) * mm});
            skLineSegment(sketch, "E355", {"start": v(0.96, 3.52) * mm, "end": v(0.79, 3.56) * mm});
            skLineSegment(sketch, "E356", {"start": v(-13.03, -13.83) * mm, "end": v(-13.07, -13.82) * mm});
            skLineSegment(sketch, "E357", {"start": v(10.52, -13.83) * mm, "end": v(10.48, -13.82) * mm});
            skLineSegment(sketch, "E358", {"start": v(-10.48, -9.73) * mm, "end": v(-10.52, -9.72) * mm});
            skLineSegment(sketch, "E359", {"start": v(13.07, -9.73) * mm, "end": v(13.03, -9.72) * mm});
            skLineSegment(sketch, "E360", {"start": v(10.52, 9.72) * mm, "end": v(10.48, 9.73) * mm});
            skLineSegment(sketch, "E361", {"start": v(-13.03, 9.72) * mm, "end": v(-13.07, 9.73) * mm});
            skLineSegment(sketch, "E362", {"start": v(13.07, 13.82) * mm, "end": v(13.03, 13.83) * mm});
            skLineSegment(sketch, "E363", {"start": v(-10.48, 13.82) * mm, "end": v(-10.52, 13.83) * mm});
            skLineSegment(sketch, "E364", {"start": v(-13.36, -14.97) * mm, "end": v(-13.45, -14.95) * mm});
            skLineSegment(sketch, "E365", {"start": v(13.45, 14.95) * mm, "end": v(13.36, 14.97) * mm});
            skLineSegment(sketch, "E366", {"start": v(-0.61, -3.6) * mm, "end": v(-0.79, -3.56) * mm});
            skLineSegment(sketch, "E367", {"start": v(0.79, 3.56) * mm, "end": v(0.61, 3.6) * mm});
            skLineSegment(sketch, "E368", {"start": v(10.57, -13.84) * mm, "end": v(10.52, -13.83) * mm});
            skLineSegment(sketch, "E369", {"start": v(-10.52, -9.72) * mm, "end": v(-10.57, -9.7) * mm});
            skLineSegment(sketch, "E370", {"start": v(10.57, 9.7) * mm, "end": v(10.52, 9.72) * mm});
            skLineSegment(sketch, "E371", {"start": v(-10.52, 13.83) * mm, "end": v(-10.57, 13.84) * mm});
            skLineSegment(sketch, "E372", {"start": v(-13.27, -14.98) * mm, "end": v(-13.36, -14.97) * mm});
            skLineSegment(sketch, "E373", {"start": v(13.36, 14.97) * mm, "end": v(13.27, 14.98) * mm});
            skLineSegment(sketch, "E374", {"start": v(-12.98, -13.84) * mm, "end": v(-13.03, -13.83) * mm});
            skLineSegment(sketch, "E375", {"start": v(13.03, -9.72) * mm, "end": v(12.98, -9.7) * mm});
            skLineSegment(sketch, "E376", {"start": v(-12.98, 9.7) * mm, "end": v(-13.03, 9.72) * mm});
            skLineSegment(sketch, "E377", {"start": v(13.03, 13.83) * mm, "end": v(12.98, 13.84) * mm});
            skLineSegment(sketch, "E378", {"start": v(-0.44, -3.62) * mm, "end": v(-0.61, -3.6) * mm});
            skLineSegment(sketch, "E379", {"start": v(0.61, 3.6) * mm, "end": v(0.44, 3.62) * mm});
            skLineSegment(sketch, "E380", {"start": v(12.98, -9.7) * mm, "end": v(12.94, -9.7) * mm});
            skLineSegment(sketch, "E381", {"start": v(-12.94, 9.7) * mm, "end": v(-12.98, 9.7) * mm});
            skLineSegment(sketch, "E382", {"start": v(-10.57, -9.7) * mm, "end": v(-10.61, -9.7) * mm});
            skLineSegment(sketch, "E383", {"start": v(10.61, 9.7) * mm, "end": v(10.57, 9.7) * mm});
            skLineSegment(sketch, "E384", {"start": v(-13.18, -15) * mm, "end": v(-13.27, -14.98) * mm});
            skLineSegment(sketch, "E385", {"start": v(13.27, 14.98) * mm, "end": v(13.18, 15) * mm});
            skLineSegment(sketch, "E386", {"start": v(-12.94, -13.85) * mm, "end": v(-12.98, -13.84) * mm});
            skLineSegment(sketch, "E387", {"start": v(12.98, 13.84) * mm, "end": v(12.94, 13.85) * mm});
            skLineSegment(sketch, "E388", {"start": v(10.61, -13.85) * mm, "end": v(10.57, -13.84) * mm});
            skLineSegment(sketch, "E389", {"start": v(-10.57, 13.84) * mm, "end": v(-10.61, 13.85) * mm});
            skLineSegment(sketch, "E390", {"start": v(-0.26, -3.64) * mm, "end": v(-0.44, -3.62) * mm});
            skLineSegment(sketch, "E391", {"start": v(0.44, 3.62) * mm, "end": v(0.26, 3.64) * mm});
            skLineSegment(sketch, "E392", {"start": v(-13.09, -15) * mm, "end": v(-13.18, -15) * mm});
            skLineSegment(sketch, "E393", {"start": v(-12.9, -13.85) * mm, "end": v(-12.94, -13.85) * mm});
            skLineSegment(sketch, "E394", {"start": v(10.66, -13.85) * mm, "end": v(10.61, -13.85) * mm});
            skLineSegment(sketch, "E395", {"start": v(12.94, 13.85) * mm, "end": v(12.9, 13.85) * mm});
            skLineSegment(sketch, "E396", {"start": v(-10.61, 13.85) * mm, "end": v(-10.66, 13.85) * mm});
            skLineSegment(sketch, "E397", {"start": v(13.18, 15) * mm, "end": v(13.09, 15) * mm});
            skLineSegment(sketch, "E398", {"start": v(-10.61, -9.7) * mm, "end": v(-10.66, -9.7) * mm});
            skLineSegment(sketch, "E399", {"start": v(12.94, -9.7) * mm, "end": v(12.9, -9.7) * mm});
            skLineSegment(sketch, "E400", {"start": v(10.66, 9.7) * mm, "end": v(10.61, 9.7) * mm});
            skLineSegment(sketch, "E401", {"start": v(-12.9, 9.7) * mm, "end": v(-12.94, 9.7) * mm});
            skLineSegment(sketch, "E402", {"start": v(-0.09, -3.65) * mm, "end": v(-0.26, -3.64) * mm});
            skLineSegment(sketch, "E403", {"start": v(0.26, 3.64) * mm, "end": v(0.09, 3.65) * mm});
            skLineSegment(sketch, "E404", {"start": v(-13, -15) * mm, "end": v(-13.09, -15) * mm});
            skLineSegment(sketch, "E405", {"start": v(-12.85, -13.85) * mm, "end": v(-12.9, -13.85) * mm});
            skLineSegment(sketch, "E406", {"start": v(10.7, -13.85) * mm, "end": v(10.66, -13.85) * mm});
            skLineSegment(sketch, "E407", {"start": v(-10.66, -9.7) * mm, "end": v(-10.7, -9.7) * mm});
            skLineSegment(sketch, "E408", {"start": v(12.9, -9.7) * mm, "end": v(12.85, -9.7) * mm});
            skLineSegment(sketch, "E409", {"start": v(10.7, 9.7) * mm, "end": v(10.66, 9.7) * mm});
            skLineSegment(sketch, "E410", {"start": v(-12.85, 9.7) * mm, "end": v(-12.9, 9.7) * mm});
            skLineSegment(sketch, "E411", {"start": v(12.9, 13.85) * mm, "end": v(12.85, 13.85) * mm});
            skLineSegment(sketch, "E412", {"start": v(-10.66, 13.85) * mm, "end": v(-10.7, 13.85) * mm});
            skLineSegment(sketch, "E413", {"start": v(13.09, 15) * mm, "end": v(13, 15) * mm});
            skLineSegment(sketch, "E414", {"start": v(8.25, -12.8) * mm, "end": v(4, -12.8) * mm});
            skLineSegment(sketch, "E415", {"start": v(-4, 12.8) * mm, "end": v(-8.25, 12.8) * mm});
            skLineSegment(sketch, "E416", {"start": v(-13, -15) * mm, "end": v(-4.5, -15) * mm});
            skLineSegment(sketch, "E417", {"start": v(4.5, -15) * mm, "end": v(13, -15) * mm});
            skLineSegment(sketch, "E418", {"start": v(-4.5, -14.5) * mm, "end": v(-4, -14.5) * mm});
            skLineSegment(sketch, "E419", {"start": v(4, -14.5) * mm, "end": v(4.5, -14.5) * mm});
            skLineSegment(sketch, "E420", {"start": v(-12.85, -13.85) * mm, "end": v(-10.7, -13.85) * mm});
            skLineSegment(sketch, "E421", {"start": v(10.7, -13.85) * mm, "end": v(12.85, -13.85) * mm});
            skLineSegment(sketch, "E422", {"start": v(-12.85, -9.7) * mm, "end": v(-10.7, -9.7) * mm});
            skLineSegment(sketch, "E423", {"start": v(10.7, -9.7) * mm, "end": v(12.85, -9.7) * mm});
            skLineSegment(sketch, "E424", {"start": v(-12.8, -8.25) * mm, "end": v(-10.05, -8.25) * mm});
            skLineSegment(sketch, "E425", {"start": v(10.05, -8.25) * mm, "end": v(12.8, -8.25) * mm});
            skLineSegment(sketch, "E426", {"start": v(-4.2, -6) * mm, "end": v(-0.92, -6) * mm});
            skLineSegment(sketch, "E427", {"start": v(0.92, -6) * mm, "end": v(4.2, -6) * mm});
            skLineSegment(sketch, "E428", {"start": v(-15, -4.5) * mm, "end": v(-14.5, -4.5) * mm});
            skLineSegment(sketch, "E429", {"start": v(14.5, -4.5) * mm, "end": v(15, -4.5) * mm});
            skLineSegment(sketch, "E430", {"start": v(-14.5, -4) * mm, "end": v(-12.8, -4) * mm});
            skLineSegment(sketch, "E431", {"start": v(12.8, -4) * mm, "end": v(14.5, -4) * mm});
            skLineSegment(sketch, "E432", {"start": v(-0.09, -3.65) * mm, "end": v(0.09, -3.65) * mm});
            skLineSegment(sketch, "E433", {"start": v(-0.09, 3.65) * mm, "end": v(0.09, 3.65) * mm});
            skLineSegment(sketch, "E434", {"start": v(12.8, 4) * mm, "end": v(14.5, 4) * mm});
            skLineSegment(sketch, "E435", {"start": v(-14.5, 4) * mm, "end": v(-12.8, 4) * mm});
            skLineSegment(sketch, "E436", {"start": v(14.5, 4.5) * mm, "end": v(15, 4.5) * mm});
            skLineSegment(sketch, "E437", {"start": v(0.92, 6) * mm, "end": v(4.2, 6) * mm});
            skLineSegment(sketch, "E438", {"start": v(-4.2, 6) * mm, "end": v(-0.92, 6) * mm});
            skLineSegment(sketch, "E439", {"start": v(10.05, 8.25) * mm, "end": v(12.8, 8.25) * mm});
            skLineSegment(sketch, "E440", {"start": v(-12.8, 8.25) * mm, "end": v(-10.05, 8.25) * mm});
            skLineSegment(sketch, "E441", {"start": v(10.7, 9.7) * mm, "end": v(12.85, 9.7) * mm});
            skLineSegment(sketch, "E442", {"start": v(-12.85, 9.7) * mm, "end": v(-10.7, 9.7) * mm});
            skLineSegment(sketch, "E443", {"start": v(10.7, 13.85) * mm, "end": v(12.85, 13.85) * mm});
            skLineSegment(sketch, "E444", {"start": v(-12.85, 13.85) * mm, "end": v(-10.7, 13.85) * mm});
            skLineSegment(sketch, "E445", {"start": v(4, 14.5) * mm, "end": v(4.5, 14.5) * mm});
            skLineSegment(sketch, "E446", {"start": v(-4.5, 14.5) * mm, "end": v(-4, 14.5) * mm});
            skLineSegment(sketch, "E447", {"start": v(4.5, 15) * mm, "end": v(13, 15) * mm});
            skLineSegment(sketch, "E448", {"start": v(-13, 15) * mm, "end": v(-4.5, 15) * mm});
            skLineSegment(sketch, "E449", {"start": v(-8.25, -12.8) * mm, "end": v(-4, -12.8) * mm});
            skLineSegment(sketch, "E450", {"start": v(4, 12.8) * mm, "end": v(8.25, 12.8) * mm});
            skLineSegment(sketch, "E451", {"start": v(13, -15) * mm, "end": v(13.09, -15) * mm});
            skLineSegment(sketch, "E452", {"start": v(-10.7, -13.85) * mm, "end": v(-10.66, -13.85) * mm});
            skLineSegment(sketch, "E453", {"start": v(12.85, -13.85) * mm, "end": v(12.9, -13.85) * mm});
            skLineSegment(sketch, "E454", {"start": v(-12.9, -9.7) * mm, "end": v(-12.85, -9.7) * mm});
            skLineSegment(sketch, "E455", {"start": v(10.66, -9.7) * mm, "end": v(10.7, -9.7) * mm});
            skLineSegment(sketch, "E456", {"start": v(12.85, 9.7) * mm, "end": v(12.9, 9.7) * mm});
            skLineSegment(sketch, "E457", {"start": v(-10.7, 9.7) * mm, "end": v(-10.66, 9.7) * mm});
            skLineSegment(sketch, "E458", {"start": v(10.66, 13.85) * mm, "end": v(10.7, 13.85) * mm});
            skLineSegment(sketch, "E459", {"start": v(-12.9, 13.85) * mm, "end": v(-12.85, 13.85) * mm});
            skLineSegment(sketch, "E460", {"start": v(-13.09, 15) * mm, "end": v(-13, 15) * mm});
            skLineSegment(sketch, "E461", {"start": v(0.09, -3.65) * mm, "end": v(0.26, -3.64) * mm});
            skLineSegment(sketch, "E462", {"start": v(-0.26, 3.64) * mm, "end": v(-0.09, 3.65) * mm});
            skLineSegment(sketch, "E463", {"start": v(-12.94, -9.7) * mm, "end": v(-12.9, -9.7) * mm});
            skLineSegment(sketch, "E464", {"start": v(10.61, -9.7) * mm, "end": v(10.66, -9.7) * mm});
            skLineSegment(sketch, "E465", {"start": v(12.9, 9.7) * mm, "end": v(12.94, 9.7) * mm});
            skLineSegment(sketch, "E466", {"start": v(-10.66, 9.7) * mm, "end": v(-10.61, 9.7) * mm});
            skLineSegment(sketch, "E467", {"start": v(13.09, -15) * mm, "end": v(13.18, -15) * mm});
            skLineSegment(sketch, "E468", {"start": v(-10.66, -13.85) * mm, "end": v(-10.61, -13.85) * mm});
            skLineSegment(sketch, "E469", {"start": v(12.9, -13.85) * mm, "end": v(12.94, -13.85) * mm});
            skLineSegment(sketch, "E470", {"start": v(10.61, 13.85) * mm, "end": v(10.66, 13.85) * mm});
            skLineSegment(sketch, "E471", {"start": v(-12.94, 13.85) * mm, "end": v(-12.9, 13.85) * mm});
            skLineSegment(sketch, "E472", {"start": v(-13.18, 15) * mm, "end": v(-13.09, 15) * mm});
            skLineSegment(sketch, "E473", {"start": v(0.26, -3.64) * mm, "end": v(0.44, -3.62) * mm});
            skLineSegment(sketch, "E474", {"start": v(-0.44, 3.62) * mm, "end": v(-0.26, 3.64) * mm});
            skLineSegment(sketch, "E475", {"start": v(-10.61, -13.85) * mm, "end": v(-10.57, -13.84) * mm});
            skLineSegment(sketch, "E476", {"start": v(10.57, 13.84) * mm, "end": v(10.61, 13.85) * mm});
            skLineSegment(sketch, "E477", {"start": v(12.94, -13.85) * mm, "end": v(12.98, -13.84) * mm});
            skLineSegment(sketch, "E478", {"start": v(-12.98, 13.84) * mm, "end": v(-12.94, 13.85) * mm});
            skLineSegment(sketch, "E479", {"start": v(13.18, -15) * mm, "end": v(13.27, -14.98) * mm});
            skLineSegment(sketch, "E480", {"start": v(-13.27, 14.98) * mm, "end": v(-13.18, 15) * mm});
            skLineSegment(sketch, "E481", {"start": v(10.57, -9.7) * mm, "end": v(10.61, -9.7) * mm});
            skLineSegment(sketch, "E482", {"start": v(-10.61, 9.7) * mm, "end": v(-10.57, 9.7) * mm});
            skLineSegment(sketch, "E483", {"start": v(-12.98, -9.7) * mm, "end": v(-12.94, -9.7) * mm});
            skLineSegment(sketch, "E484", {"start": v(12.94, 9.7) * mm, "end": v(12.98, 9.7) * mm});
            skLineSegment(sketch, "E485", {"start": v(0.44, -3.62) * mm, "end": v(0.61, -3.6) * mm});
            skLineSegment(sketch, "E486", {"start": v(-0.61, 3.6) * mm, "end": v(-0.44, 3.62) * mm});
            skLineSegment(sketch, "E487", {"start": v(12.98, -13.84) * mm, "end": v(13.03, -13.83) * mm});
            skLineSegment(sketch, "E488", {"start": v(-13.03, -9.72) * mm, "end": v(-12.98, -9.7) * mm});
            skLineSegment(sketch, "E489", {"start": v(12.98, 9.7) * mm, "end": v(13.03, 9.72) * mm});
            skLineSegment(sketch, "E490", {"start": v(-13.03, 13.83) * mm, "end": v(-12.98, 13.84) * mm});
            skLineSegment(sketch, "E491", {"start": v(13.27, -14.98) * mm, "end": v(13.36, -14.97) * mm});
            skLineSegment(sketch, "E492", {"start": v(-13.36, 14.97) * mm, "end": v(-13.27, 14.98) * mm});
            skLineSegment(sketch, "E493", {"start": v(-10.57, -13.84) * mm, "end": v(-10.52, -13.83) * mm});
            skLineSegment(sketch, "E494", {"start": v(10.52, -9.72) * mm, "end": v(10.57, -9.7) * mm});
            skLineSegment(sketch, "E495", {"start": v(-10.57, 9.7) * mm, "end": v(-10.52, 9.72) * mm});
            skLineSegment(sketch, "E496", {"start": v(10.52, 13.83) * mm, "end": v(10.57, 13.84) * mm});
            skLineSegment(sketch, "E497", {"start": v(0.61, -3.6) * mm, "end": v(0.79, -3.56) * mm});
            skLineSegment(sketch, "E498", {"start": v(-0.79, 3.56) * mm, "end": v(-0.61, 3.6) * mm});
            skLineSegment(sketch, "E499", {"start": v(13.36, -14.97) * mm, "end": v(13.45, -14.95) * mm});
            skLineSegment(sketch, "E500", {"start": v(-13.45, 14.95) * mm, "end": v(-13.36, 14.97) * mm});
            skLineSegment(sketch, "E501", {"start": v(-10.52, -13.83) * mm, "end": v(-10.48, -13.82) * mm});
            skLineSegment(sketch, "E502", {"start": v(13.03, -13.83) * mm, "end": v(13.07, -13.82) * mm});
            skLineSegment(sketch, "E503", {"start": v(-13.07, -9.73) * mm, "end": v(-13.03, -9.72) * mm});
            skLineSegment(sketch, "E504", {"start": v(10.48, -9.73) * mm, "end": v(10.52, -9.72) * mm});
            skLineSegment(sketch, "E505", {"start": v(13.03, 9.72) * mm, "end": v(13.07, 9.73) * mm});
            skLineSegment(sketch, "E506", {"start": v(-10.52, 9.72) * mm, "end": v(-10.48, 9.73) * mm});
            skLineSegment(sketch, "E507", {"start": v(10.48, 13.82) * mm, "end": v(10.52, 13.83) * mm});
            skLineSegment(sketch, "E508", {"start": v(-13.07, 13.82) * mm, "end": v(-13.03, 13.83) * mm});
            skLineSegment(sketch, "E509", {"start": v(0.79, -3.56) * mm, "end": v(0.96, -3.52) * mm});
            skLineSegment(sketch, "E510", {"start": v(-0.96, 3.52) * mm, "end": v(-0.79, 3.56) * mm});
            skLineSegment(sketch, "E511", {"start": v(13.45, -14.95) * mm, "end": v(13.53, -14.93) * mm});
            skLineSegment(sketch, "E512", {"start": v(-10.48, -13.82) * mm, "end": v(-10.43, -13.81) * mm});
            skLineSegment(sketch, "E513", {"start": v(10.43, -9.74) * mm, "end": v(10.48, -9.73) * mm});
            skLineSegment(sketch, "E514", {"start": v(-10.48, 9.73) * mm, "end": v(-10.43, 9.74) * mm});
            skLineSegment(sketch, "E515", {"start": v(10.43, 13.81) * mm, "end": v(10.48, 13.82) * mm});
            skLineSegment(sketch, "E516", {"start": v(-13.53, 14.93) * mm, "end": v(-13.45, 14.95) * mm});
            skLineSegment(sketch, "E517", {"start": v(13.07, -13.82) * mm, "end": v(13.12, -13.81) * mm});
            skLineSegment(sketch, "E518", {"start": v(-13.12, -9.74) * mm, "end": v(-13.07, -9.73) * mm});
            skLineSegment(sketch, "E519", {"start": v(13.07, 9.73) * mm, "end": v(13.12, 9.74) * mm});
            skLineSegment(sketch, "E520", {"start": v(-13.12, 13.81) * mm, "end": v(-13.07, 13.82) * mm});
            skLineSegment(sketch, "E521", {"start": v(0.96, -3.52) * mm, "end": v(1.13, -3.47) * mm});
            skLineSegment(sketch, "E522", {"start": v(-1.13, 3.47) * mm, "end": v(-0.96, 3.52) * mm});
            skLineSegment(sketch, "E523", {"start": v(13.12, -13.81) * mm, "end": v(13.16, -13.8) * mm});
            skLineSegment(sketch, "E524", {"start": v(-13.16, -9.75) * mm, "end": v(-13.12, -9.74) * mm});
            skLineSegment(sketch, "E525", {"start": v(13.12, 9.74) * mm, "end": v(13.16, 9.75) * mm});
            skLineSegment(sketch, "E526", {"start": v(-13.16, 13.8) * mm, "end": v(-13.12, 13.81) * mm});
            skLineSegment(sketch, "E527", {"start": v(-10.43, -13.81) * mm, "end": v(-10.4, -13.8) * mm});
            skLineSegment(sketch, "E528", {"start": v(10.4, -9.75) * mm, "end": v(10.43, -9.74) * mm});
            skLineSegment(sketch, "E529", {"start": v(-10.43, 9.74) * mm, "end": v(-10.4, 9.75) * mm});
            skLineSegment(sketch, "E530", {"start": v(10.4, 13.8) * mm, "end": v(10.43, 13.81) * mm});
            skLineSegment(sketch, "E531", {"start": v(13.53, -14.93) * mm, "end": v(13.62, -14.9) * mm});
            skLineSegment(sketch, "E532", {"start": v(-13.62, 14.9) * mm, "end": v(-13.53, 14.93) * mm});
            skLineSegment(sketch, "E533", {"start": v(13.62, -14.9) * mm, "end": v(13.7, -14.87) * mm});
            skLineSegment(sketch, "E534", {"start": v(-13.7, 14.87) * mm, "end": v(-13.62, 14.9) * mm});
            skLineSegment(sketch, "E535", {"start": v(-10.4, -13.8) * mm, "end": v(-10.35, -13.79) * mm});
            skLineSegment(sketch, "E536", {"start": v(13.16, -13.8) * mm, "end": v(13.2, -13.79) * mm});
            skLineSegment(sketch, "E537", {"start": v(-13.2, -9.76) * mm, "end": v(-13.16, -9.75) * mm});
            skLineSegment(sketch, "E538", {"start": v(10.35, -9.76) * mm, "end": v(10.4, -9.75) * mm});
            skLineSegment(sketch, "E539", {"start": v(13.16, 9.75) * mm, "end": v(13.2, 9.76) * mm});
            skLineSegment(sketch, "E540", {"start": v(-10.4, 9.75) * mm, "end": v(-10.35, 9.76) * mm});
            skLineSegment(sketch, "E541", {"start": v(10.35, 13.79) * mm, "end": v(10.4, 13.8) * mm});
            skLineSegment(sketch, "E542", {"start": v(-13.2, 13.79) * mm, "end": v(-13.16, 13.8) * mm});
            skLineSegment(sketch, "E543", {"start": v(1.13, -3.47) * mm, "end": v(1.3, -3.41) * mm});
            skLineSegment(sketch, "E544", {"start": v(-1.3, 3.41) * mm, "end": v(-1.13, 3.47) * mm});
            skLineSegment(sketch, "E545", {"start": v(13.7, -14.87) * mm, "end": v(13.79, -14.84) * mm});
            skLineSegment(sketch, "E546", {"start": v(-13.79, 14.84) * mm, "end": v(-13.7, 14.87) * mm});
            skLineSegment(sketch, "E547", {"start": v(-13.24, -9.78) * mm, "end": v(-13.2, -9.76) * mm});
            skLineSegment(sketch, "E548", {"start": v(10.3, -9.78) * mm, "end": v(10.35, -9.76) * mm});
            skLineSegment(sketch, "E549", {"start": v(13.2, 9.76) * mm, "end": v(13.24, 9.78) * mm});
            skLineSegment(sketch, "E550", {"start": v(-10.35, 9.76) * mm, "end": v(-10.3, 9.78) * mm});
            skLineSegment(sketch, "E551", {"start": v(-10.35, -13.79) * mm, "end": v(-10.3, -13.77) * mm});
            skLineSegment(sketch, "E552", {"start": v(13.2, -13.79) * mm, "end": v(13.24, -13.77) * mm});
            skLineSegment(sketch, "E553", {"start": v(10.3, 13.77) * mm, "end": v(10.35, 13.79) * mm});
            skLineSegment(sketch, "E554", {"start": v(-13.24, 13.77) * mm, "end": v(-13.2, 13.79) * mm});
            skLineSegment(sketch, "E555", {"start": v(1.3, -3.41) * mm, "end": v(1.46, -3.35) * mm});
            skLineSegment(sketch, "E556", {"start": v(-1.46, 3.35) * mm, "end": v(-1.3, 3.41) * mm});
            skLineSegment(sketch, "E557", {"start": v(-10.3, -13.77) * mm, "end": v(-10.27, -13.75) * mm});
            skLineSegment(sketch, "E558", {"start": v(13.24, -13.77) * mm, "end": v(13.28, -13.75) * mm});
            skLineSegment(sketch, "E559", {"start": v(10.27, 13.75) * mm, "end": v(10.3, 13.77) * mm});
            skLineSegment(sketch, "E560", {"start": v(-13.28, 13.75) * mm, "end": v(-13.24, 13.77) * mm});
            skLineSegment(sketch, "E561", {"start": v(-13.28, -9.8) * mm, "end": v(-13.24, -9.78) * mm});
            skLineSegment(sketch, "E562", {"start": v(10.27, -9.8) * mm, "end": v(10.3, -9.78) * mm});
            skLineSegment(sketch, "E563", {"start": v(13.24, 9.78) * mm, "end": v(13.28, 9.8) * mm});
            skLineSegment(sketch, "E564", {"start": v(-10.3, 9.78) * mm, "end": v(-10.27, 9.8) * mm});
            skLineSegment(sketch, "E565", {"start": v(13.79, -14.84) * mm, "end": v(13.87, -14.8) * mm});
            skLineSegment(sketch, "E566", {"start": v(-13.87, 14.8) * mm, "end": v(-13.79, 14.84) * mm});
            skLineSegment(sketch, "E567", {"start": v(1.46, -3.35) * mm, "end": v(1.62, -3.27) * mm});
            skLineSegment(sketch, "E568", {"start": v(-1.62, 3.27) * mm, "end": v(-1.46, 3.35) * mm});
            skLineSegment(sketch, "E569", {"start": v(-10.27, -13.75) * mm, "end": v(-10.23, -13.73) * mm});
            skLineSegment(sketch, "E570", {"start": v(13.28, -13.75) * mm, "end": v(13.32, -13.73) * mm});
            skLineSegment(sketch, "E571", {"start": v(10.23, 13.73) * mm, "end": v(10.27, 13.75) * mm});
            skLineSegment(sketch, "E572", {"start": v(-13.32, 13.73) * mm, "end": v(-13.28, 13.75) * mm});
            skLineSegment(sketch, "E573", {"start": v(13.87, -14.8) * mm, "end": v(13.95, -14.76) * mm});
            skLineSegment(sketch, "E574", {"start": v(-13.95, 14.76) * mm, "end": v(-13.87, 14.8) * mm});
            skLineSegment(sketch, "E575", {"start": v(-13.32, -9.82) * mm, "end": v(-13.28, -9.8) * mm});
            skLineSegment(sketch, "E576", {"start": v(10.23, -9.82) * mm, "end": v(10.27, -9.8) * mm});
            skLineSegment(sketch, "E577", {"start": v(13.28, 9.8) * mm, "end": v(13.32, 9.82) * mm});
            skLineSegment(sketch, "E578", {"start": v(-10.27, 9.8) * mm, "end": v(-10.23, 9.82) * mm});
            skLineSegment(sketch, "E579", {"start": v(10.19, -9.84) * mm, "end": v(10.23, -9.82) * mm});
            skLineSegment(sketch, "E580", {"start": v(-10.23, 9.82) * mm, "end": v(-10.19, 9.84) * mm});
            skLineSegment(sketch, "E581", {"start": v(-13.36, -9.84) * mm, "end": v(-13.32, -9.82) * mm});
            skLineSegment(sketch, "E582", {"start": v(13.32, 9.82) * mm, "end": v(13.36, 9.84) * mm});
            skLineSegment(sketch, "E583", {"start": v(13.95, -14.76) * mm, "end": v(14.03, -14.72) * mm});
            skLineSegment(sketch, "E584", {"start": v(-14.03, 14.72) * mm, "end": v(-13.95, 14.76) * mm});
            skLineSegment(sketch, "E585", {"start": v(-10.23, -13.73) * mm, "end": v(-10.19, -13.7) * mm});
            skLineSegment(sketch, "E586", {"start": v(10.19, 13.7) * mm, "end": v(10.23, 13.73) * mm});
            skLineSegment(sketch, "E587", {"start": v(13.32, -13.73) * mm, "end": v(13.36, -13.7) * mm});
            skLineSegment(sketch, "E588", {"start": v(-13.36, 13.7) * mm, "end": v(-13.32, 13.73) * mm});
            skLineSegment(sketch, "E589", {"start": v(-0.92, -6) * mm, "end": v(0, -5.47) * mm});
            skLineSegment(sketch, "E590", {"start": v(0, 5.47) * mm, "end": v(0.92, 6) * mm});
            skLineSegment(sketch, "E591", {"start": v(13.36, -13.7) * mm, "end": v(13.4, -13.68) * mm});
            skLineSegment(sketch, "E592", {"start": v(-13.4, 13.68) * mm, "end": v(-13.36, 13.7) * mm});
            skLineSegment(sketch, "E593", {"start": v(-10.19, -13.7) * mm, "end": v(-10.15, -13.68) * mm});
            skLineSegment(sketch, "E594", {"start": v(10.15, 13.68) * mm, "end": v(10.19, 13.7) * mm});
            skLineSegment(sketch, "E595", {"start": v(14.03, -14.72) * mm, "end": v(14.1, -14.67) * mm});
            skLineSegment(sketch, "E596", {"start": v(-14.1, 14.67) * mm, "end": v(-14.03, 14.72) * mm});
            skLineSegment(sketch, "E597", {"start": v(-13.4, -9.87) * mm, "end": v(-13.36, -9.84) * mm});
            skLineSegment(sketch, "E598", {"start": v(13.36, 9.84) * mm, "end": v(13.4, 9.87) * mm});
            skLineSegment(sketch, "E599", {"start": v(10.15, -9.87) * mm, "end": v(10.19, -9.84) * mm});
            skLineSegment(sketch, "E600", {"start": v(-10.19, 9.84) * mm, "end": v(-10.15, 9.87) * mm});
            skLineSegment(sketch, "E601", {"start": v(-10.15, -13.68) * mm, "end": v(-10.11, -13.66) * mm});
            skLineSegment(sketch, "E602", {"start": v(13.4, -13.68) * mm, "end": v(13.44, -13.66) * mm});
            skLineSegment(sketch, "E603", {"start": v(-13.44, -9.9) * mm, "end": v(-13.4, -9.87) * mm});
            skLineSegment(sketch, "E604", {"start": v(10.11, -9.9) * mm, "end": v(10.15, -9.87) * mm});
            skLineSegment(sketch, "E605", {"start": v(13.4, 9.87) * mm, "end": v(13.44, 9.9) * mm});
            skLineSegment(sketch, "E606", {"start": v(-10.15, 9.87) * mm, "end": v(-10.11, 9.9) * mm});
            skLineSegment(sketch, "E607", {"start": v(10.11, 13.66) * mm, "end": v(10.15, 13.68) * mm});
            skLineSegment(sketch, "E608", {"start": v(-13.44, 13.66) * mm, "end": v(-13.4, 13.68) * mm});
            skLineSegment(sketch, "E609", {"start": v(14.1, -14.67) * mm, "end": v(14.18, -14.62) * mm});
            skLineSegment(sketch, "E610", {"start": v(-14.18, 14.62) * mm, "end": v(-14.1, 14.67) * mm});
            skLineSegment(sketch, "E611", {"start": v(3.12, -4.53) * mm, "end": v(3.35, -4.36) * mm});
            skLineSegment(sketch, "E612", {"start": v(-3.35, 4.36) * mm, "end": v(-3.12, 4.53) * mm});
            skLineSegment(sketch, "E613", {"start": v(-13.47, -9.92) * mm, "end": v(-13.44, -9.9) * mm});
            skLineSegment(sketch, "E614", {"start": v(10.08, -9.92) * mm, "end": v(10.11, -9.9) * mm});
            skLineSegment(sketch, "E615", {"start": v(13.44, 9.9) * mm, "end": v(13.47, 9.92) * mm});
            skLineSegment(sketch, "E616", {"start": v(-10.11, 9.9) * mm, "end": v(-10.08, 9.92) * mm});
            skLineSegment(sketch, "E617", {"start": v(14.18, -14.62) * mm, "end": v(14.25, -14.56) * mm});
            skLineSegment(sketch, "E618", {"start": v(-14.25, 14.56) * mm, "end": v(-14.18, 14.62) * mm});
            skLineSegment(sketch, "E619", {"start": v(-10.11, -13.66) * mm, "end": v(-10.08, -13.63) * mm});
            skLineSegment(sketch, "E620", {"start": v(13.44, -13.66) * mm, "end": v(13.47, -13.63) * mm});
            skLineSegment(sketch, "E621", {"start": v(10.08, 13.63) * mm, "end": v(10.11, 13.66) * mm});
            skLineSegment(sketch, "E622", {"start": v(-13.47, 13.63) * mm, "end": v(-13.44, 13.66) * mm});
            skLineSegment(sketch, "E623", {"start": v(3.35, -4.36) * mm, "end": v(3.57, -4.18) * mm});
            skLineSegment(sketch, "E624", {"start": v(-3.57, 4.18) * mm, "end": v(-3.35, 4.36) * mm});
            skLineSegment(sketch, "E625", {"start": v(14.25, -14.56) * mm, "end": v(14.32, -14.5) * mm});
            skLineSegment(sketch, "E626", {"start": v(-10.08, -13.63) * mm, "end": v(-10.04, -13.6) * mm});
            skLineSegment(sketch, "E627", {"start": v(10.04, 13.6) * mm, "end": v(10.08, 13.63) * mm});
            skLineSegment(sketch, "E628", {"start": v(-14.32, 14.5) * mm, "end": v(-14.25, 14.56) * mm});
            skLineSegment(sketch, "E629", {"start": v(13.47, -13.63) * mm, "end": v(13.5, -13.6) * mm});
            skLineSegment(sketch, "E630", {"start": v(-13.5, 13.6) * mm, "end": v(-13.47, 13.63) * mm});
            skLineSegment(sketch, "E631", {"start": v(10.04, -9.95) * mm, "end": v(10.08, -9.92) * mm});
            skLineSegment(sketch, "E632", {"start": v(-10.08, 9.92) * mm, "end": v(-10.04, 9.95) * mm});
            skLineSegment(sketch, "E633", {"start": v(-13.5, -9.95) * mm, "end": v(-13.47, -9.92) * mm});
            skLineSegment(sketch, "E634", {"start": v(13.47, 9.92) * mm, "end": v(13.5, 9.95) * mm});
            skLineSegment(sketch, "E635", {"start": v(-3.12, -4.53) * mm, "end": v(-1.62, -3.27) * mm});
            skLineSegment(sketch, "E636", {"start": v(1.62, 3.27) * mm, "end": v(3.12, 4.53) * mm});
            skLineSegment(sketch, "E637", {"start": v(3.57, -4.18) * mm, "end": v(3.79, -3.99) * mm});
            skLineSegment(sketch, "E638", {"start": v(-3.79, 3.99) * mm, "end": v(-3.57, 4.18) * mm});
            skLineSegment(sketch, "E639", {"start": v(-10.04, -13.6) * mm, "end": v(-10, -13.57) * mm});
            skLineSegment(sketch, "E640", {"start": v(13.5, -13.6) * mm, "end": v(13.54, -13.57) * mm});
            skLineSegment(sketch, "E641", {"start": v(-13.54, -9.98) * mm, "end": v(-13.5, -9.95) * mm});
            skLineSegment(sketch, "E642", {"start": v(10, -9.98) * mm, "end": v(10.04, -9.95) * mm});
            skLineSegment(sketch, "E643", {"start": v(13.5, 9.95) * mm, "end": v(13.54, 9.98) * mm});
            skLineSegment(sketch, "E644", {"start": v(-10.04, 9.95) * mm, "end": v(-10, 9.98) * mm});
            skLineSegment(sketch, "E645", {"start": v(10, 13.57) * mm, "end": v(10.04, 13.6) * mm});
            skLineSegment(sketch, "E646", {"start": v(-13.54, 13.57) * mm, "end": v(-13.5, 13.6) * mm});
            skLineSegment(sketch, "E647", {"start": v(14.32, -14.5) * mm, "end": v(14.38, -14.45) * mm});
            skLineSegment(sketch, "E648", {"start": v(-14.38, 14.45) * mm, "end": v(-14.32, 14.5) * mm});
            skLineSegment(sketch, "E649", {"start": v(-13.57, -10) * mm, "end": v(-13.54, -9.98) * mm});
            skLineSegment(sketch, "E650", {"start": v(13.54, 9.98) * mm, "end": v(13.57, 10) * mm});
            skLineSegment(sketch, "E651", {"start": v(14.38, -14.45) * mm, "end": v(14.45, -14.38) * mm});
            skLineSegment(sketch, "E652", {"start": v(13.54, -13.57) * mm, "end": v(13.57, -13.54) * mm});
            skLineSegment(sketch, "E653", {"start": v(-8.25, -10.05) * mm, "end": v(-4.2, -6) * mm});
            skLineSegment(sketch, "E654", {"start": v(9.98, -10) * mm, "end": v(10, -9.98) * mm});
            skLineSegment(sketch, "E655", {"start": v(-10.05, -8.25) * mm, "end": v(-6, -4.2) * mm});
            skLineSegment(sketch, "E656", {"start": v(3.79, -3.99) * mm, "end": v(3.99, -3.79) * mm});
            skLineSegment(sketch, "E657", {"start": v(-3.99, 3.79) * mm, "end": v(-3.79, 3.99) * mm});
            skLineSegment(sketch, "E658", {"start": v(6, 4.2) * mm, "end": v(10.05, 8.25) * mm});
            skLineSegment(sketch, "E659", {"start": v(4.2, 6) * mm, "end": v(8.25, 10.05) * mm});
            skLineSegment(sketch, "E660", {"start": v(-10, 9.98) * mm, "end": v(-9.98, 10) * mm});
            skLineSegment(sketch, "E661", {"start": v(-13.57, 13.54) * mm, "end": v(-13.54, 13.57) * mm});
            skLineSegment(sketch, "E662", {"start": v(-14.45, 14.38) * mm, "end": v(-14.38, 14.45) * mm});
            skLineSegment(sketch, "E663", {"start": v(-10, -13.57) * mm, "end": v(-9.98, -13.54) * mm});
            skLineSegment(sketch, "E664", {"start": v(9.98, 13.54) * mm, "end": v(10, 13.57) * mm});
            skLineSegment(sketch, "E665", {"start": v(14.45, -14.38) * mm, "end": v(14.5, -14.32) * mm});
            skLineSegment(sketch, "E666", {"start": v(-14.5, 14.32) * mm, "end": v(-14.45, 14.38) * mm});
            skLineSegment(sketch, "E667", {"start": v(-9.98, -13.54) * mm, "end": v(-9.95, -13.5) * mm});
            skLineSegment(sketch, "E668", {"start": v(13.57, -13.54) * mm, "end": v(13.6, -13.5) * mm});
            skLineSegment(sketch, "E669", {"start": v(-13.6, -10.04) * mm, "end": v(-13.57, -10) * mm});
            skLineSegment(sketch, "E670", {"start": v(9.95, -10.04) * mm, "end": v(9.98, -10) * mm});
            skLineSegment(sketch, "E671", {"start": v(13.57, 10) * mm, "end": v(13.6, 10.04) * mm});
            skLineSegment(sketch, "E672", {"start": v(-9.98, 10) * mm, "end": v(-9.95, 10.04) * mm});
            skLineSegment(sketch, "E673", {"start": v(9.95, 13.5) * mm, "end": v(9.98, 13.54) * mm});
            skLineSegment(sketch, "E674", {"start": v(-13.6, 13.5) * mm, "end": v(-13.57, 13.54) * mm});
            skLineSegment(sketch, "E675", {"start": v(3.99, -3.79) * mm, "end": v(4.18, -3.57) * mm});
            skLineSegment(sketch, "E676", {"start": v(-4.18, 3.57) * mm, "end": v(-3.99, 3.79) * mm});
            skLineSegment(sketch, "E677", {"start": v(-4.53, -3.12) * mm, "end": v(-3.27, -1.62) * mm});
            skLineSegment(sketch, "E678", {"start": v(3.27, 1.62) * mm, "end": v(4.53, 3.12) * mm});
            skLineSegment(sketch, "E679", {"start": v(-9.95, -13.5) * mm, "end": v(-9.92, -13.47) * mm});
            skLineSegment(sketch, "E680", {"start": v(9.92, 13.47) * mm, "end": v(9.95, 13.5) * mm});
            skLineSegment(sketch, "E681", {"start": v(9.92, -10.08) * mm, "end": v(9.95, -10.04) * mm});
            skLineSegment(sketch, "E682", {"start": v(-9.95, 10.04) * mm, "end": v(-9.92, 10.08) * mm});
            skLineSegment(sketch, "E683", {"start": v(13.6, -13.5) * mm, "end": v(13.63, -13.47) * mm});
            skLineSegment(sketch, "E684", {"start": v(-13.63, 13.47) * mm, "end": v(-13.6, 13.5) * mm});
            skLineSegment(sketch, "E685", {"start": v(14.5, -14.32) * mm, "end": v(14.56, -14.25) * mm});
            skLineSegment(sketch, "E686", {"start": v(-13.63, -10.08) * mm, "end": v(-13.6, -10.04) * mm});
            skLineSegment(sketch, "E687", {"start": v(13.6, 10.04) * mm, "end": v(13.63, 10.08) * mm});
            skLineSegment(sketch, "E688", {"start": v(-14.56, 14.25) * mm, "end": v(-14.5, 14.32) * mm});
            skLineSegment(sketch, "E689", {"start": v(4.18, -3.57) * mm, "end": v(4.36, -3.35) * mm});
            skLineSegment(sketch, "E690", {"start": v(-4.36, 3.35) * mm, "end": v(-4.18, 3.57) * mm});
            skLineSegment(sketch, "E691", {"start": v(13.63, -13.47) * mm, "end": v(13.66, -13.44) * mm});
            skLineSegment(sketch, "E692", {"start": v(-13.66, -10.11) * mm, "end": v(-13.63, -10.08) * mm});
            skLineSegment(sketch, "E693", {"start": v(13.63, 10.08) * mm, "end": v(13.66, 10.11) * mm});
            skLineSegment(sketch, "E694", {"start": v(-13.66, 13.44) * mm, "end": v(-13.63, 13.47) * mm});
            skLineSegment(sketch, "E695", {"start": v(14.56, -14.25) * mm, "end": v(14.62, -14.18) * mm});
            skLineSegment(sketch, "E696", {"start": v(-14.62, 14.18) * mm, "end": v(-14.56, 14.25) * mm});
            skLineSegment(sketch, "E697", {"start": v(-9.92, -13.47) * mm, "end": v(-9.9, -13.44) * mm});
            skLineSegment(sketch, "E698", {"start": v(9.9, -10.11) * mm, "end": v(9.92, -10.08) * mm});
            skLineSegment(sketch, "E699", {"start": v(-9.92, 10.08) * mm, "end": v(-9.9, 10.11) * mm});
            skLineSegment(sketch, "E700", {"start": v(9.9, 13.44) * mm, "end": v(9.92, 13.47) * mm});
            skLineSegment(sketch, "E701", {"start": v(4.36, -3.35) * mm, "end": v(4.53, -3.12) * mm});
            skLineSegment(sketch, "E702", {"start": v(-4.53, 3.12) * mm, "end": v(-4.36, 3.35) * mm});
            skLineSegment(sketch, "E703", {"start": v(14.62, -14.18) * mm, "end": v(14.67, -14.1) * mm});
            skLineSegment(sketch, "E704", {"start": v(-14.67, 14.1) * mm, "end": v(-14.62, 14.18) * mm});
            skLineSegment(sketch, "E705", {"start": v(-9.9, -13.44) * mm, "end": v(-9.87, -13.4) * mm});
            skLineSegment(sketch, "E706", {"start": v(13.66, -13.44) * mm, "end": v(13.68, -13.4) * mm});
            skLineSegment(sketch, "E707", {"start": v(-13.68, -10.15) * mm, "end": v(-13.66, -10.11) * mm});
            skLineSegment(sketch, "E708", {"start": v(9.87, -10.15) * mm, "end": v(9.9, -10.11) * mm});
            skLineSegment(sketch, "E709", {"start": v(13.66, 10.11) * mm, "end": v(13.68, 10.15) * mm});
            skLineSegment(sketch, "E710", {"start": v(-9.9, 10.11) * mm, "end": v(-9.87, 10.15) * mm});
            skLineSegment(sketch, "E711", {"start": v(9.87, 13.4) * mm, "end": v(9.9, 13.44) * mm});
            skLineSegment(sketch, "E712", {"start": v(-13.68, 13.4) * mm, "end": v(-13.66, 13.44) * mm});
            skLineSegment(sketch, "E713", {"start": v(9.84, -10.19) * mm, "end": v(9.87, -10.15) * mm});
            skLineSegment(sketch, "E714", {"start": v(-9.87, 10.15) * mm, "end": v(-9.84, 10.19) * mm});
            skLineSegment(sketch, "E715", {"start": v(-9.87, -13.4) * mm, "end": v(-9.84, -13.36) * mm});
            skLineSegment(sketch, "E716", {"start": v(9.84, 13.36) * mm, "end": v(9.87, 13.4) * mm});
            skLineSegment(sketch, "E717", {"start": v(14.67, -14.1) * mm, "end": v(14.72, -14.03) * mm});
            skLineSegment(sketch, "E718", {"start": v(-14.72, 14.03) * mm, "end": v(-14.67, 14.1) * mm});
            skLineSegment(sketch, "E719", {"start": v(-13.7, -10.19) * mm, "end": v(-13.68, -10.15) * mm});
            skLineSegment(sketch, "E720", {"start": v(13.68, 10.15) * mm, "end": v(13.7, 10.19) * mm});
            skLineSegment(sketch, "E721", {"start": v(13.68, -13.4) * mm, "end": v(13.7, -13.36) * mm});
            skLineSegment(sketch, "E722", {"start": v(-13.7, 13.36) * mm, "end": v(-13.68, 13.4) * mm});
            skLineSegment(sketch, "E723", {"start": v(-6, -0.92) * mm, "end": v(-5.47, 0) * mm});
            skLineSegment(sketch, "E724", {"start": v(5.47, 0) * mm, "end": v(6, 0.92) * mm});
            skLineSegment(sketch, "E725", {"start": v(13.7, -13.36) * mm, "end": v(13.73, -13.32) * mm});
            skLineSegment(sketch, "E726", {"start": v(-13.73, 13.32) * mm, "end": v(-13.7, 13.36) * mm});
            skLineSegment(sketch, "E727", {"start": v(-13.73, -10.23) * mm, "end": v(-13.7, -10.19) * mm});
            skLineSegment(sketch, "E728", {"start": v(13.7, 10.19) * mm, "end": v(13.73, 10.23) * mm});
            skLineSegment(sketch, "E729", {"start": v(14.72, -14.03) * mm, "end": v(14.76, -13.95) * mm});
            skLineSegment(sketch, "E730", {"start": v(-14.76, 13.95) * mm, "end": v(-14.72, 14.03) * mm});
            skLineSegment(sketch, "E731", {"start": v(-9.84, -13.36) * mm, "end": v(-9.82, -13.32) * mm});
            skLineSegment(sketch, "E732", {"start": v(9.82, 13.32) * mm, "end": v(9.84, 13.36) * mm});
            skLineSegment(sketch, "E733", {"start": v(9.82, -10.23) * mm, "end": v(9.84, -10.19) * mm});
            skLineSegment(sketch, "E734", {"start": v(-9.84, 10.19) * mm, "end": v(-9.82, 10.23) * mm});
            skLineSegment(sketch, "E735", {"start": v(-9.82, -13.32) * mm, "end": v(-9.8, -13.28) * mm});
            skLineSegment(sketch, "E736", {"start": v(9.8, -10.27) * mm, "end": v(9.82, -10.23) * mm});
            skLineSegment(sketch, "E737", {"start": v(-9.82, 10.23) * mm, "end": v(-9.8, 10.27) * mm});
            skLineSegment(sketch, "E738", {"start": v(9.8, 13.28) * mm, "end": v(9.82, 13.32) * mm});
            skLineSegment(sketch, "E739", {"start": v(14.76, -13.95) * mm, "end": v(14.8, -13.87) * mm});
            skLineSegment(sketch, "E740", {"start": v(-14.8, 13.87) * mm, "end": v(-14.76, 13.95) * mm});
            skLineSegment(sketch, "E741", {"start": v(13.73, -13.32) * mm, "end": v(13.75, -13.28) * mm});
            skLineSegment(sketch, "E742", {"start": v(-13.75, -10.27) * mm, "end": v(-13.73, -10.23) * mm});
            skLineSegment(sketch, "E743", {"start": v(13.73, 10.23) * mm, "end": v(13.75, 10.27) * mm});
            skLineSegment(sketch, "E744", {"start": v(-13.75, 13.28) * mm, "end": v(-13.73, 13.32) * mm});
            skLineSegment(sketch, "E745", {"start": v(3.27, -1.62) * mm, "end": v(3.35, -1.46) * mm});
            skLineSegment(sketch, "E746", {"start": v(-3.35, 1.46) * mm, "end": v(-3.27, 1.62) * mm});
            skLineSegment(sketch, "E747", {"start": v(14.8, -13.87) * mm, "end": v(14.84, -13.79) * mm});
            skLineSegment(sketch, "E748", {"start": v(-14.84, 13.79) * mm, "end": v(-14.8, 13.87) * mm});
            skLineSegment(sketch, "E749", {"start": v(-9.8, -13.28) * mm, "end": v(-9.78, -13.24) * mm});
            skLineSegment(sketch, "E750", {"start": v(9.78, -10.3) * mm, "end": v(9.8, -10.27) * mm});
            skLineSegment(sketch, "E751", {"start": v(-9.8, 10.27) * mm, "end": v(-9.78, 10.3) * mm});
            skLineSegment(sketch, "E752", {"start": v(9.78, 13.24) * mm, "end": v(9.8, 13.28) * mm});
            skLineSegment(sketch, "E753", {"start": v(13.75, -13.28) * mm, "end": v(13.77, -13.24) * mm});
            skLineSegment(sketch, "E754", {"start": v(-13.77, -10.3) * mm, "end": v(-13.75, -10.27) * mm});
            skLineSegment(sketch, "E755", {"start": v(13.75, 10.27) * mm, "end": v(13.77, 10.3) * mm});
            skLineSegment(sketch, "E756", {"start": v(-13.77, 13.24) * mm, "end": v(-13.75, 13.28) * mm});
            skLineSegment(sketch, "E757", {"start": v(3.35, -1.46) * mm, "end": v(3.41, -1.3) * mm});
            skLineSegment(sketch, "E758", {"start": v(-3.41, 1.3) * mm, "end": v(-3.35, 1.46) * mm});
            skLineSegment(sketch, "E759", {"start": v(13.77, -13.24) * mm, "end": v(13.79, -13.2) * mm});
            skLineSegment(sketch, "E760", {"start": v(-13.79, -10.35) * mm, "end": v(-13.77, -10.3) * mm});
            skLineSegment(sketch, "E761", {"start": v(13.77, 10.3) * mm, "end": v(13.79, 10.35) * mm});
            skLineSegment(sketch, "E762", {"start": v(-13.79, 13.2) * mm, "end": v(-13.77, 13.24) * mm});
            skLineSegment(sketch, "E763", {"start": v(-9.78, -13.24) * mm, "end": v(-9.76, -13.2) * mm});
            skLineSegment(sketch, "E764", {"start": v(9.76, -10.35) * mm, "end": v(9.78, -10.3) * mm});
            skLineSegment(sketch, "E765", {"start": v(-9.78, 10.3) * mm, "end": v(-9.76, 10.35) * mm});
            skLineSegment(sketch, "E766", {"start": v(9.76, 13.2) * mm, "end": v(9.78, 13.24) * mm});
            skLineSegment(sketch, "E767", {"start": v(14.84, -13.79) * mm, "end": v(14.87, -13.7) * mm});
            skLineSegment(sketch, "E768", {"start": v(-14.87, 13.7) * mm, "end": v(-14.84, 13.79) * mm});
            skLineSegment(sketch, "E769", {"start": v(3.41, -1.3) * mm, "end": v(3.47, -1.13) * mm});
            skLineSegment(sketch, "E770", {"start": v(-3.47, 1.13) * mm, "end": v(-3.41, 1.3) * mm});
            skLineSegment(sketch, "E771", {"start": v(-9.76, -13.2) * mm, "end": v(-9.75, -13.16) * mm});
            skLineSegment(sketch, "E772", {"start": v(13.79, -13.2) * mm, "end": v(13.8, -13.16) * mm});
            skLineSegment(sketch, "E773", {"start": v(-13.8, -10.4) * mm, "end": v(-13.79, -10.35) * mm});
            skLineSegment(sketch, "E774", {"start": v(9.75, -10.4) * mm, "end": v(9.76, -10.35) * mm});
            skLineSegment(sketch, "E775", {"start": v(13.79, 10.35) * mm, "end": v(13.8, 10.4) * mm});
            skLineSegment(sketch, "E776", {"start": v(-9.76, 10.35) * mm, "end": v(-9.75, 10.4) * mm});
            skLineSegment(sketch, "E777", {"start": v(9.75, 13.16) * mm, "end": v(9.76, 13.2) * mm});
            skLineSegment(sketch, "E778", {"start": v(-13.8, 13.16) * mm, "end": v(-13.79, 13.2) * mm});
            skLineSegment(sketch, "E779", {"start": v(14.87, -13.7) * mm, "end": v(14.9, -13.62) * mm});
            skLineSegment(sketch, "E780", {"start": v(-14.9, 13.62) * mm, "end": v(-14.87, 13.7) * mm});
            skLineSegment(sketch, "E781", {"start": v(14.9, -13.62) * mm, "end": v(14.93, -13.53) * mm});
            skLineSegment(sketch, "E782", {"start": v(-14.93, 13.53) * mm, "end": v(-14.9, 13.62) * mm});
            skLineSegment(sketch, "E783", {"start": v(-13.81, -10.43) * mm, "end": v(-13.8, -10.4) * mm});
            skLineSegment(sketch, "E784", {"start": v(9.74, -10.43) * mm, "end": v(9.75, -10.4) * mm});
            skLineSegment(sketch, "E785", {"start": v(13.8, 10.4) * mm, "end": v(13.81, 10.43) * mm});
            skLineSegment(sketch, "E786", {"start": v(-9.75, 10.4) * mm, "end": v(-9.74, 10.43) * mm});
            skLineSegment(sketch, "E787", {"start": v(-9.75, -13.16) * mm, "end": v(-9.74, -13.12) * mm});
            skLineSegment(sketch, "E788", {"start": v(13.8, -13.16) * mm, "end": v(13.81, -13.12) * mm});
            skLineSegment(sketch, "E789", {"start": v(9.74, 13.12) * mm, "end": v(9.75, 13.16) * mm});
            skLineSegment(sketch, "E790", {"start": v(-13.81, 13.12) * mm, "end": v(-13.8, 13.16) * mm});
            skLineSegment(sketch, "E791", {"start": v(3.47, -1.13) * mm, "end": v(3.52, -0.96) * mm});
            skLineSegment(sketch, "E792", {"start": v(-3.52, 0.96) * mm, "end": v(-3.47, 1.13) * mm});
            skLineSegment(sketch, "E793", {"start": v(-9.74, -13.12) * mm, "end": v(-9.73, -13.07) * mm});
            skLineSegment(sketch, "E794", {"start": v(13.81, -13.12) * mm, "end": v(13.82, -13.07) * mm});
            skLineSegment(sketch, "E795", {"start": v(9.73, 13.07) * mm, "end": v(9.74, 13.12) * mm});
            skLineSegment(sketch, "E796", {"start": v(-13.82, 13.07) * mm, "end": v(-13.81, 13.12) * mm});
            skLineSegment(sketch, "E797", {"start": v(14.93, -13.53) * mm, "end": v(14.95, -13.45) * mm});
            skLineSegment(sketch, "E798", {"start": v(-13.82, -10.48) * mm, "end": v(-13.81, -10.43) * mm});
            skLineSegment(sketch, "E799", {"start": v(9.73, -10.48) * mm, "end": v(9.74, -10.43) * mm});
            skLineSegment(sketch, "E800", {"start": v(13.81, 10.43) * mm, "end": v(13.82, 10.48) * mm});
            skLineSegment(sketch, "E801", {"start": v(-9.74, 10.43) * mm, "end": v(-9.73, 10.48) * mm});
            skLineSegment(sketch, "E802", {"start": v(-14.95, 13.45) * mm, "end": v(-14.93, 13.53) * mm});
            skLineSegment(sketch, "E803", {"start": v(3.52, -0.96) * mm, "end": v(3.56, -0.79) * mm});
            skLineSegment(sketch, "E804", {"start": v(-3.56, 0.79) * mm, "end": v(-3.52, 0.96) * mm});
            skLineSegment(sketch, "E805", {"start": v(-9.73, -13.07) * mm, "end": v(-9.72, -13.03) * mm});
            skLineSegment(sketch, "E806", {"start": v(13.82, -13.07) * mm, "end": v(13.83, -13.03) * mm});
            skLineSegment(sketch, "E807", {"start": v(-13.83, -10.52) * mm, "end": v(-13.82, -10.48) * mm});
            skLineSegment(sketch, "E808", {"start": v(9.72, -10.52) * mm, "end": v(9.73, -10.48) * mm});
            skLineSegment(sketch, "E809", {"start": v(13.82, 10.48) * mm, "end": v(13.83, 10.52) * mm});
            skLineSegment(sketch, "E810", {"start": v(-9.73, 10.48) * mm, "end": v(-9.72, 10.52) * mm});
            skLineSegment(sketch, "E811", {"start": v(9.72, 13.03) * mm, "end": v(9.73, 13.07) * mm});
            skLineSegment(sketch, "E812", {"start": v(-13.83, 13.03) * mm, "end": v(-13.82, 13.07) * mm});
            skLineSegment(sketch, "E813", {"start": v(14.95, -13.45) * mm, "end": v(14.97, -13.36) * mm});
            skLineSegment(sketch, "E814", {"start": v(-14.97, 13.36) * mm, "end": v(-14.95, 13.45) * mm});
            skLineSegment(sketch, "E815", {"start": v(3.56, -0.79) * mm, "end": v(3.6, -0.61) * mm});
            skLineSegment(sketch, "E816", {"start": v(-3.6, 0.61) * mm, "end": v(-3.56, 0.79) * mm});
            skLineSegment(sketch, "E817", {"start": v(-13.84, -10.57) * mm, "end": v(-13.83, -10.52) * mm});
            skLineSegment(sketch, "E818", {"start": v(9.7, -10.57) * mm, "end": v(9.72, -10.52) * mm});
            skLineSegment(sketch, "E819", {"start": v(13.83, 10.52) * mm, "end": v(13.84, 10.57) * mm});
            skLineSegment(sketch, "E820", {"start": v(-9.72, 10.52) * mm, "end": v(-9.7, 10.57) * mm});
            skLineSegment(sketch, "E821", {"start": v(14.97, -13.36) * mm, "end": v(14.98, -13.27) * mm});
            skLineSegment(sketch, "E822", {"start": v(-14.98, 13.27) * mm, "end": v(-14.97, 13.36) * mm});
            skLineSegment(sketch, "E823", {"start": v(-9.72, -13.03) * mm, "end": v(-9.7, -12.98) * mm});
            skLineSegment(sketch, "E824", {"start": v(13.83, -13.03) * mm, "end": v(13.84, -12.98) * mm});
            skLineSegment(sketch, "E825", {"start": v(9.7, 12.98) * mm, "end": v(9.72, 13.03) * mm});
            skLineSegment(sketch, "E826", {"start": v(-13.84, 12.98) * mm, "end": v(-13.83, 13.03) * mm});
            skLineSegment(sketch, "E827", {"start": v(3.6, -0.61) * mm, "end": v(3.62, -0.44) * mm});
            skLineSegment(sketch, "E828", {"start": v(-3.62, 0.44) * mm, "end": v(-3.6, 0.61) * mm});
            skLineSegment(sketch, "E829", {"start": v(-9.7, -12.98) * mm, "end": v(-9.7, -12.94) * mm});
            skLineSegment(sketch, "E830", {"start": v(9.7, 12.94) * mm, "end": v(9.7, 12.98) * mm});
            skLineSegment(sketch, "E831", {"start": v(9.7, -10.61) * mm, "end": v(9.7, -10.57) * mm});
            skLineSegment(sketch, "E832", {"start": v(-9.7, 10.57) * mm, "end": v(-9.7, 10.61) * mm});
            skLineSegment(sketch, "E833", {"start": v(14.98, -13.27) * mm, "end": v(15, -13.18) * mm});
            skLineSegment(sketch, "E834", {"start": v(-15, 13.18) * mm, "end": v(-14.98, 13.27) * mm});
            skLineSegment(sketch, "E835", {"start": v(13.84, -12.98) * mm, "end": v(13.85, -12.94) * mm});
            skLineSegment(sketch, "E836", {"start": v(-13.85, 12.94) * mm, "end": v(-13.84, 12.98) * mm});
            skLineSegment(sketch, "E837", {"start": v(-13.85, -10.61) * mm, "end": v(-13.84, -10.57) * mm});
            skLineSegment(sketch, "E838", {"start": v(13.84, 10.57) * mm, "end": v(13.85, 10.61) * mm});
            skLineSegment(sketch, "E839", {"start": v(3.62, -0.44) * mm, "end": v(3.64, -0.26) * mm});
            skLineSegment(sketch, "E840", {"start": v(-3.64, 0.26) * mm, "end": v(-3.62, 0.44) * mm});
            skLineSegment(sketch, "E841", {"start": v(13.85, -12.94) * mm, "end": v(13.85, -12.9) * mm});
            skLineSegment(sketch, "E842", {"start": v(-13.85, -10.66) * mm, "end": v(-13.85, -10.61) * mm});
            skLineSegment(sketch, "E843", {"start": v(13.85, 10.61) * mm, "end": v(13.85, 10.66) * mm});
            skLineSegment(sketch, "E844", {"start": v(-13.85, 12.9) * mm, "end": v(-13.85, 12.94) * mm});
            skLineSegment(sketch, "E845", {"start": v(15, -13.18) * mm, "end": v(15, -13.09) * mm});
            skLineSegment(sketch, "E846", {"start": v(-15, 13.09) * mm, "end": v(-15, 13.18) * mm});
            skLineSegment(sketch, "E847", {"start": v(-9.7, -12.94) * mm, "end": v(-9.7, -12.9) * mm});
            skLineSegment(sketch, "E848", {"start": v(9.7, -10.66) * mm, "end": v(9.7, -10.61) * mm});
            skLineSegment(sketch, "E849", {"start": v(-9.7, 10.61) * mm, "end": v(-9.7, 10.66) * mm});
            skLineSegment(sketch, "E850", {"start": v(9.7, 12.9) * mm, "end": v(9.7, 12.94) * mm});
            skLineSegment(sketch, "E851", {"start": v(3.64, -0.26) * mm, "end": v(3.65, -0.09) * mm});
            skLineSegment(sketch, "E852", {"start": v(-3.65, 0.09) * mm, "end": v(-3.64, 0.26) * mm});
            skLineSegment(sketch, "E853", {"start": v(15, -13.09) * mm, "end": v(15, -13) * mm});
            skLineSegment(sketch, "E854", {"start": v(-15, 13) * mm, "end": v(-15, 13.09) * mm});
            skLineSegment(sketch, "E855", {"start": v(-9.7, -12.9) * mm, "end": v(-9.7, -12.85) * mm});
            skLineSegment(sketch, "E856", {"start": v(13.85, -12.9) * mm, "end": v(13.85, -12.85) * mm});
            skLineSegment(sketch, "E857", {"start": v(-13.85, -10.7) * mm, "end": v(-13.85, -10.66) * mm});
            skLineSegment(sketch, "E858", {"start": v(9.7, -10.7) * mm, "end": v(9.7, -10.66) * mm});
            skLineSegment(sketch, "E859", {"start": v(13.85, 10.66) * mm, "end": v(13.85, 10.7) * mm});
            skLineSegment(sketch, "E860", {"start": v(-9.7, 10.66) * mm, "end": v(-9.7, 10.7) * mm});
            skLineSegment(sketch, "E861", {"start": v(9.7, 12.85) * mm, "end": v(9.7, 12.9) * mm});
            skLineSegment(sketch, "E862", {"start": v(-13.85, 12.85) * mm, "end": v(-13.85, 12.9) * mm});
            skLineSegment(sketch, "E863", {"start": v(-12.8, -8.25) * mm, "end": v(-12.8, -4) * mm});
            skLineSegment(sketch, "E864", {"start": v(12.8, 4) * mm, "end": v(12.8, 8.25) * mm});
            skLineSegment(sketch, "E865", {"start": v(-15, 4.5) * mm, "end": v(-15, 13) * mm});
            skLineSegment(sketch, "E866", {"start": v(-15, -13) * mm, "end": v(-15, -4.5) * mm});
            skLineSegment(sketch, "E867", {"start": v(-14.5, -4.5) * mm, "end": v(-14.5, -4) * mm});
            skLineSegment(sketch, "E868", {"start": v(-13.85, -12.85) * mm, "end": v(-13.85, -10.7) * mm});
            skLineSegment(sketch, "E869", {"start": v(-13.85, 10.7) * mm, "end": v(-13.85, 12.85) * mm});
            skLineSegment(sketch, "E870", {"start": v(-9.7, -12.85) * mm, "end": v(-9.7, -10.7) * mm});
            skLineSegment(sketch, "E871", {"start": v(-9.7, 10.7) * mm, "end": v(-9.7, 12.85) * mm});
            skLineSegment(sketch, "E872", {"start": v(-8.25, 10.05) * mm, "end": v(-8.25, 12.8) * mm});
            skLineSegment(sketch, "E873", {"start": v(-8.25, -12.8) * mm, "end": v(-8.25, -10.05) * mm});
            skLineSegment(sketch, "E874", {"start": v(-6, 0.92) * mm, "end": v(-6, 4.2) * mm});
            skLineSegment(sketch, "E875", {"start": v(-6, -4.2) * mm, "end": v(-6, -0.92) * mm});
            skLineSegment(sketch, "E876", {"start": v(-4.5, 14.5) * mm, "end": v(-4.5, 15) * mm});
            skLineSegment(sketch, "E877", {"start": v(-4.5, -15) * mm, "end": v(-4.5, -14.5) * mm});
            skLineSegment(sketch, "E878", {"start": v(-4, 12.8) * mm, "end": v(-4, 14.5) * mm});
            skLineSegment(sketch, "E879", {"start": v(-4, -14.5) * mm, "end": v(-4, -12.8) * mm});
            skLineSegment(sketch, "E880", {"start": v(-3.65, -0.09) * mm, "end": v(-3.65, 0.09) * mm});
            skLineSegment(sketch, "E881", {"start": v(3.65, -0.09) * mm, "end": v(3.65, 0.09) * mm});
            skLineSegment(sketch, "E882", {"start": v(4, 12.8) * mm, "end": v(4, 14.5) * mm});
            skLineSegment(sketch, "E883", {"start": v(4, -14.5) * mm, "end": v(4, -12.8) * mm});
            skLineSegment(sketch, "E884", {"start": v(4.5, 14.5) * mm, "end": v(4.5, 15) * mm});
            skLineSegment(sketch, "E885", {"start": v(4.5, -15) * mm, "end": v(4.5, -14.5) * mm});
            skLineSegment(sketch, "E886", {"start": v(6, 0.92) * mm, "end": v(6, 4.2) * mm});
            skLineSegment(sketch, "E887", {"start": v(6, -4.2) * mm, "end": v(6, -0.92) * mm});
            skLineSegment(sketch, "E888", {"start": v(8.25, 10.05) * mm, "end": v(8.25, 12.8) * mm});
            skLineSegment(sketch, "E889", {"start": v(8.25, -12.8) * mm, "end": v(8.25, -10.05) * mm});
            skLineSegment(sketch, "E890", {"start": v(9.7, -12.85) * mm, "end": v(9.7, -10.7) * mm});
            skLineSegment(sketch, "E891", {"start": v(9.7, 10.7) * mm, "end": v(9.7, 12.85) * mm});
            skLineSegment(sketch, "E892", {"start": v(13.85, -12.85) * mm, "end": v(13.85, -10.7) * mm});
            skLineSegment(sketch, "E893", {"start": v(13.85, 10.7) * mm, "end": v(13.85, 12.85) * mm});
            skLineSegment(sketch, "E894", {"start": v(14.5, 4) * mm, "end": v(14.5, 4.5) * mm});
            skLineSegment(sketch, "E895", {"start": v(14.5, -4.5) * mm, "end": v(14.5, -4) * mm});
            skLineSegment(sketch, "E896", {"start": v(15, 4.5) * mm, "end": v(15, 13) * mm});
            skLineSegment(sketch, "E897", {"start": v(15, -13) * mm, "end": v(15, -4.5) * mm});
            skLineSegment(sketch, "E898", {"start": v(4, 14.5) * mm, "end": v(4.5, 15) * mm});
            skLineSegment(sketch, "E899", {"start": v(-4.5, 15) * mm, "end": v(-4, 14.5) * mm});
            skLineSegment(sketch, "E900", {"start": v(14.5, 4) * mm, "end": v(15, 4.5) * mm});
            skLineSegment(sketch, "E901", {"start": v(14.5, -4) * mm, "end": v(15, -4.5) * mm});
            skLineSegment(sketch, "E902", {"start": v(4.5, -15) * mm, "end": v(4, -14.5) * mm});
            skLineSegment(sketch, "E903", {"start": v(-4.5, -15) * mm, "end": v(-4, -14.5) * mm});
            skLineSegment(sketch, "E904", {"start": v(-15, -4.5) * mm, "end": v(-14.5, -4) * mm});
            skLineSegment(sketch, "E905", {"start": v(-15, 4.5) * mm, "end": v(-14.5, 4) * mm});
            skSolve(sketch);
        }
        {
            var Q0;
            Q0=makeQuery(id+"F0.imprint","IMPRINT",FACE,{"disambiguationData":[TD([[makeQuery(id+"F0.imprint","IMPRINT",EDGE,{"derivedFrom":sQuery(id+"F0.wireOp",EDGE,"E0")}),-1.0]])]});
            extrude(context, id + "F1", {"entities" : qUnion([Q0]), "depth" : 500 * mm, "offsetDistance" : 25 * mm});
        }
    });
